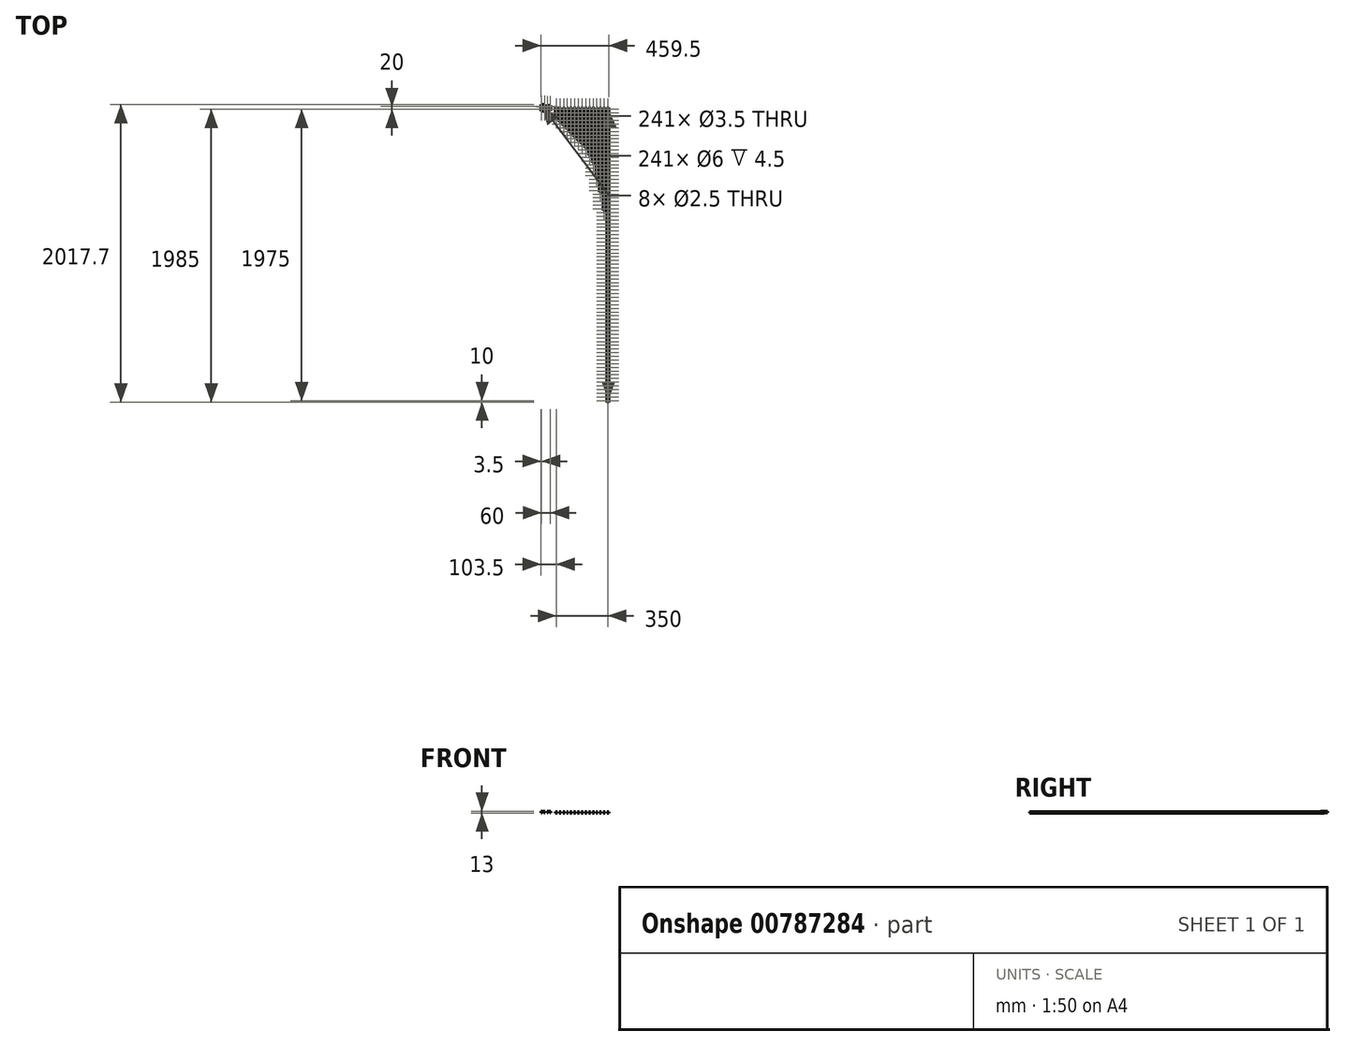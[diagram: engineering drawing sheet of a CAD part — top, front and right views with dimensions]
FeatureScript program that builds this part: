
annotation { "Feature Type Name" : "Feature", "Feature Type Description" : "" }
export const myFeature = defineFeature(function(context is Context, id is Id, definition is map)
    precondition{}
    {
        {
            var Q0;
            Q0=qCreatedBy(makeId("Front.planeOp"),FACE);
            var sketch = newSketch(context, id + "F0", { "sketchPlane" : qUnion([Q0])});
            skPoint(sketch, "E0.middle", {"position": v(0, 0) * mm});
            skLineSegment(sketch, "E1.bottom", {"start": v(5.5, -4) * mm, "end": v(-5.5, -4) * mm});
            skLineSegment(sketch, "E1.top", {"start": v(5.5, 4) * mm, "end": v(-5.5, 4) * mm});
            skLineSegment(sketch, "E1.left", {"start": v(6, -3.5) * mm, "end": v(6, -0.03) * mm});
            skLineSegment(sketch, "E1.right", {"start": v(-6, -3.5) * mm, "end": v(-6, -0.03) * mm});
            skArc(sketch, "E2", {"start": v(-6, -0.03) * mm, "mid": v(-5.5, 0.27) * mm, "end": v(-5.15, 0.75) * mm});
            skArc(sketch, "E3", {"start": v(6, 2.63) * mm, "mid": v(5.5, 2.33) * mm, "end": v(5.15, 1.85) * mm});
            skLineSegment(sketch, "E4", {"start": v(4.45, 1.85) * mm, "end": v(5.15, 1.85) * mm});
            skLineSegment(sketch, "E5", {"start": v(4.45, 0.75) * mm, "end": v(5.15, 0.75) * mm});
            skLineSegment(sketch, "E6", {"start": v(-4.45, 0.75) * mm, "end": v(-5.15, 0.75) * mm});
            skLineSegment(sketch, "E7", {"start": v(-4.45, 1.85) * mm, "end": v(-5.15, 1.85) * mm});
            skLineSegment(sketch, "E8", {"start": v(-6, 3.5) * mm, "end": v(-5.5, 4) * mm});
            skLineSegment(sketch, "E9.MirrorCS", {"start": v(6, 3.5) * mm, "end": v(5.5, 4) * mm});
            skLineSegment(sketch, "E10.MirrorCS", {"start": v(6, -3.5) * mm, "end": v(5.5, -4) * mm});
            skLineSegment(sketch, "E11.MirrorCS", {"start": v(-6, -3.5) * mm, "end": v(-5.5, -4) * mm});
            skPoint(sketch, "E12.orphan", {"position": v(-6, 4) * mm});
            skLineSegment(sketch, "E13.trimOffspring", {"start": v(-6, 2.63) * mm, "end": v(-6, 3.5) * mm});
            skArc(sketch, "E14.trimOffspring", {"start": v(-5.15, 1.85) * mm, "mid": v(-5.5, 2.33) * mm, "end": v(-6, 2.63) * mm});
            skPoint(sketch, "E15.orphan", {"position": v(6, 4) * mm});
            skLineSegment(sketch, "E16.trimOffspring", {"start": v(6, 2.63) * mm, "end": v(6, 3.5) * mm});
            skArc(sketch, "E17.trimOffspring", {"start": v(5.15, 0.75) * mm, "mid": v(5.5, 0.27) * mm, "end": v(6, -0.03) * mm});
            skPoint(sketch, "E18.orphan", {"position": v(6, -4) * mm});
            skPoint(sketch, "E19.orphan", {"position": v(-6, -4) * mm});
            skLineSegment(sketch, "E20", {"start": v(-4.45, 1.85) * mm, "end": v(-4.45, 0.75) * mm});
            skLineSegment(sketch, "E21", {"start": v(4.45, 1.85) * mm, "end": v(4.45, 0.75) * mm});
            skLineSegment(sketch, "E22", {"start": v(-6.44, 1.3) * mm, "end": v(6.44, 1.3) * mm, "construction": true});
            skLineSegment(sketch, "E23.1.0.0", {"start": v(18.56, 1.3) * mm, "end": v(31.44, 1.3) * mm, "construction": true});
            skLineSegment(sketch, "E23.1.0.1", {"start": v(19, -3.5) * mm, "end": v(19, -0.03) * mm});
            skLineSegment(sketch, "E23.1.0.2", {"start": v(31, -3.5) * mm, "end": v(31, -0.03) * mm});
            skLineSegment(sketch, "E23.1.0.3", {"start": v(30.5, -4) * mm, "end": v(19.5, -4) * mm});
            skLineSegment(sketch, "E23.1.0.4", {"start": v(30.5, 4) * mm, "end": v(19.5, 4) * mm});
            skPoint(sketch, "E23.1.0.5", {"position": v(25, 0) * mm});
            skPoint(sketch, "E23.1.0.6", {"position": v(19, -4) * mm});
            skPoint(sketch, "E23.1.0.7", {"position": v(19, 4) * mm});
            skPoint(sketch, "E23.1.0.8", {"position": v(31, 4) * mm});
            skPoint(sketch, "E23.1.0.9", {"position": v(31, -4) * mm});
            skPoint(sketch, "E23.1.0.10", {"position": v(25, 0) * mm});
            skLineSegment(sketch, "E23.1.0.11", {"start": v(31, -3.5) * mm, "end": v(30.5, -4) * mm});
            skLineSegment(sketch, "E23.1.0.12", {"start": v(31, 3.5) * mm, "end": v(30.5, 4) * mm});
            skLineSegment(sketch, "E23.1.0.13", {"start": v(19, -3.5) * mm, "end": v(19.5, -4) * mm});
            skLineSegment(sketch, "E23.1.0.14", {"start": v(20.55, 1.85) * mm, "end": v(19.85, 1.85) * mm});
            skLineSegment(sketch, "E23.1.0.15", {"start": v(19, 2.63) * mm, "end": v(19, 3.5) * mm});
            skLineSegment(sketch, "E23.1.0.16", {"start": v(31, 2.63) * mm, "end": v(31, 3.5) * mm});
            skArc(sketch, "E23.1.0.17", {"start": v(30.15, 0.75) * mm, "mid": v(30.5, 0.27) * mm, "end": v(31, -0.03) * mm});
            skLineSegment(sketch, "E23.1.0.18", {"start": v(20.55, 1.85) * mm, "end": v(20.55, 0.75) * mm});
            skLineSegment(sketch, "E23.1.0.19", {"start": v(29.45, 0.75) * mm, "end": v(30.15, 0.75) * mm});
            skLineSegment(sketch, "E23.1.0.20", {"start": v(20.55, 0.75) * mm, "end": v(19.85, 0.75) * mm});
            skArc(sketch, "E23.1.0.21", {"start": v(19, -0.03) * mm, "mid": v(19.5, 0.27) * mm, "end": v(19.85, 0.75) * mm});
            skLineSegment(sketch, "E23.1.0.22", {"start": v(19, 3.5) * mm, "end": v(19.5, 4) * mm});
            skArc(sketch, "E23.1.0.23", {"start": v(19.85, 1.85) * mm, "mid": v(19.5, 2.33) * mm, "end": v(19, 2.63) * mm});
            skLineSegment(sketch, "E23.1.0.24", {"start": v(29.45, 1.85) * mm, "end": v(30.15, 1.85) * mm});
            skArc(sketch, "E23.1.0.25", {"start": v(31, 2.63) * mm, "mid": v(30.5, 2.33) * mm, "end": v(30.15, 1.85) * mm});
            skArc(sketch, "E23.1.0.26", {"start": v(30.15, 0.75) * mm, "mid": v(30.5, 0.27) * mm, "end": v(31, -0.03) * mm});
            skLineSegment(sketch, "E23.1.0.27", {"start": v(29.45, 1.85) * mm, "end": v(29.45, 0.75) * mm});
            skLineSegment(sketch, "E23.2.0.0", {"start": v(43.56, 1.3) * mm, "end": v(56.44, 1.3) * mm, "construction": true});
            skLineSegment(sketch, "E23.2.0.1", {"start": v(44, -3.5) * mm, "end": v(44, -0.03) * mm});
            skLineSegment(sketch, "E23.2.0.2", {"start": v(56, -3.5) * mm, "end": v(56, -0.03) * mm});
            skLineSegment(sketch, "E23.2.0.3", {"start": v(55.5, -4) * mm, "end": v(44.5, -4) * mm});
            skLineSegment(sketch, "E23.2.0.4", {"start": v(55.5, 4) * mm, "end": v(44.5, 4) * mm});
            skPoint(sketch, "E23.2.0.5", {"position": v(50, 0) * mm});
            skPoint(sketch, "E23.2.0.6", {"position": v(44, -4) * mm});
            skPoint(sketch, "E23.2.0.7", {"position": v(44, 4) * mm});
            skPoint(sketch, "E23.2.0.8", {"position": v(56, 4) * mm});
            skPoint(sketch, "E23.2.0.9", {"position": v(56, -4) * mm});
            skPoint(sketch, "E23.2.0.10", {"position": v(50, 0) * mm});
            skLineSegment(sketch, "E23.2.0.11", {"start": v(56, -3.5) * mm, "end": v(55.5, -4) * mm});
            skLineSegment(sketch, "E23.2.0.12", {"start": v(56, 3.5) * mm, "end": v(55.5, 4) * mm});
            skLineSegment(sketch, "E23.2.0.13", {"start": v(44, -3.5) * mm, "end": v(44.5, -4) * mm});
            skLineSegment(sketch, "E23.2.0.14", {"start": v(45.55, 1.85) * mm, "end": v(44.85, 1.85) * mm});
            skLineSegment(sketch, "E23.2.0.15", {"start": v(44, 2.63) * mm, "end": v(44, 3.5) * mm});
            skLineSegment(sketch, "E23.2.0.16", {"start": v(56, 2.63) * mm, "end": v(56, 3.5) * mm});
            skArc(sketch, "E23.2.0.17", {"start": v(55.15, 0.75) * mm, "mid": v(55.5, 0.27) * mm, "end": v(56, -0.03) * mm});
            skLineSegment(sketch, "E23.2.0.18", {"start": v(45.55, 1.85) * mm, "end": v(45.55, 0.75) * mm});
            skLineSegment(sketch, "E23.2.0.19", {"start": v(54.45, 0.75) * mm, "end": v(55.15, 0.75) * mm});
            skLineSegment(sketch, "E23.2.0.20", {"start": v(45.55, 0.75) * mm, "end": v(44.85, 0.75) * mm});
            skArc(sketch, "E23.2.0.21", {"start": v(44, -0.03) * mm, "mid": v(44.5, 0.27) * mm, "end": v(44.85, 0.75) * mm});
            skLineSegment(sketch, "E23.2.0.22", {"start": v(44, 3.5) * mm, "end": v(44.5, 4) * mm});
            skArc(sketch, "E23.2.0.23", {"start": v(44.85, 1.85) * mm, "mid": v(44.5, 2.33) * mm, "end": v(44, 2.63) * mm});
            skLineSegment(sketch, "E23.2.0.24", {"start": v(54.45, 1.85) * mm, "end": v(55.15, 1.85) * mm});
            skArc(sketch, "E23.2.0.25", {"start": v(56, 2.63) * mm, "mid": v(55.5, 2.33) * mm, "end": v(55.15, 1.85) * mm});
            skArc(sketch, "E23.2.0.26", {"start": v(55.15, 0.75) * mm, "mid": v(55.5, 0.27) * mm, "end": v(56, -0.03) * mm});
            skLineSegment(sketch, "E23.2.0.27", {"start": v(54.45, 1.85) * mm, "end": v(54.45, 0.75) * mm});
            skLineSegment(sketch, "E23.3.0.0", {"start": v(68.56, 1.3) * mm, "end": v(81.44, 1.3) * mm, "construction": true});
            skLineSegment(sketch, "E23.3.0.1", {"start": v(69, -3.5) * mm, "end": v(69, -0.03) * mm});
            skLineSegment(sketch, "E23.3.0.2", {"start": v(81, -3.5) * mm, "end": v(81, -0.03) * mm});
            skLineSegment(sketch, "E23.3.0.3", {"start": v(80.5, -4) * mm, "end": v(69.5, -4) * mm});
            skLineSegment(sketch, "E23.3.0.4", {"start": v(80.5, 4) * mm, "end": v(69.5, 4) * mm});
            skPoint(sketch, "E23.3.0.5", {"position": v(75, 0) * mm});
            skPoint(sketch, "E23.3.0.6", {"position": v(69, -4) * mm});
            skPoint(sketch, "E23.3.0.7", {"position": v(69, 4) * mm});
            skPoint(sketch, "E23.3.0.8", {"position": v(81, 4) * mm});
            skPoint(sketch, "E23.3.0.9", {"position": v(81, -4) * mm});
            skPoint(sketch, "E23.3.0.10", {"position": v(75, 0) * mm});
            skLineSegment(sketch, "E23.3.0.11", {"start": v(81, -3.5) * mm, "end": v(80.5, -4) * mm});
            skLineSegment(sketch, "E23.3.0.12", {"start": v(81, 3.5) * mm, "end": v(80.5, 4) * mm});
            skLineSegment(sketch, "E23.3.0.13", {"start": v(69, -3.5) * mm, "end": v(69.5, -4) * mm});
            skLineSegment(sketch, "E23.3.0.14", {"start": v(70.55, 1.85) * mm, "end": v(69.85, 1.85) * mm});
            skLineSegment(sketch, "E23.3.0.15", {"start": v(69, 2.63) * mm, "end": v(69, 3.5) * mm});
            skLineSegment(sketch, "E23.3.0.16", {"start": v(81, 2.63) * mm, "end": v(81, 3.5) * mm});
            skArc(sketch, "E23.3.0.17", {"start": v(80.15, 0.75) * mm, "mid": v(80.5, 0.27) * mm, "end": v(81, -0.03) * mm});
            skLineSegment(sketch, "E23.3.0.18", {"start": v(70.55, 1.85) * mm, "end": v(70.55, 0.75) * mm});
            skLineSegment(sketch, "E23.3.0.19", {"start": v(79.45, 0.75) * mm, "end": v(80.15, 0.75) * mm});
            skLineSegment(sketch, "E23.3.0.20", {"start": v(70.55, 0.75) * mm, "end": v(69.85, 0.75) * mm});
            skArc(sketch, "E23.3.0.21", {"start": v(69, -0.03) * mm, "mid": v(69.5, 0.27) * mm, "end": v(69.85, 0.75) * mm});
            skLineSegment(sketch, "E23.3.0.22", {"start": v(69, 3.5) * mm, "end": v(69.5, 4) * mm});
            skArc(sketch, "E23.3.0.23", {"start": v(69.85, 1.85) * mm, "mid": v(69.5, 2.33) * mm, "end": v(69, 2.63) * mm});
            skLineSegment(sketch, "E23.3.0.24", {"start": v(79.45, 1.85) * mm, "end": v(80.15, 1.85) * mm});
            skArc(sketch, "E23.3.0.25", {"start": v(81, 2.63) * mm, "mid": v(80.5, 2.33) * mm, "end": v(80.15, 1.85) * mm});
            skArc(sketch, "E23.3.0.26", {"start": v(80.15, 0.75) * mm, "mid": v(80.5, 0.27) * mm, "end": v(81, -0.03) * mm});
            skLineSegment(sketch, "E23.3.0.27", {"start": v(79.45, 1.85) * mm, "end": v(79.45, 0.75) * mm});
            skLineSegment(sketch, "E23.4.0.0", {"start": v(93.56, 1.3) * mm, "end": v(106.44, 1.3) * mm, "construction": true});
            skLineSegment(sketch, "E23.4.0.1", {"start": v(94, -3.5) * mm, "end": v(94, -0.03) * mm});
            skLineSegment(sketch, "E23.4.0.2", {"start": v(106, -3.5) * mm, "end": v(106, -0.03) * mm});
            skLineSegment(sketch, "E23.4.0.3", {"start": v(105.5, -4) * mm, "end": v(94.5, -4) * mm});
            skLineSegment(sketch, "E23.4.0.4", {"start": v(105.5, 4) * mm, "end": v(94.5, 4) * mm});
            skPoint(sketch, "E23.4.0.5", {"position": v(100, 0) * mm});
            skPoint(sketch, "E23.4.0.6", {"position": v(94, -4) * mm});
            skPoint(sketch, "E23.4.0.7", {"position": v(94, 4) * mm});
            skPoint(sketch, "E23.4.0.8", {"position": v(106, 4) * mm});
            skPoint(sketch, "E23.4.0.9", {"position": v(106, -4) * mm});
            skPoint(sketch, "E23.4.0.10", {"position": v(100, 0) * mm});
            skLineSegment(sketch, "E23.4.0.11", {"start": v(106, -3.5) * mm, "end": v(105.5, -4) * mm});
            skLineSegment(sketch, "E23.4.0.12", {"start": v(106, 3.5) * mm, "end": v(105.5, 4) * mm});
            skLineSegment(sketch, "E23.4.0.13", {"start": v(94, -3.5) * mm, "end": v(94.5, -4) * mm});
            skLineSegment(sketch, "E23.4.0.14", {"start": v(95.55, 1.85) * mm, "end": v(94.85, 1.85) * mm});
            skLineSegment(sketch, "E23.4.0.15", {"start": v(94, 2.63) * mm, "end": v(94, 3.5) * mm});
            skLineSegment(sketch, "E23.4.0.16", {"start": v(106, 2.63) * mm, "end": v(106, 3.5) * mm});
            skArc(sketch, "E23.4.0.17", {"start": v(105.15, 0.75) * mm, "mid": v(105.5, 0.27) * mm, "end": v(106, -0.03) * mm});
            skLineSegment(sketch, "E23.4.0.18", {"start": v(95.55, 1.85) * mm, "end": v(95.55, 0.75) * mm});
            skLineSegment(sketch, "E23.4.0.19", {"start": v(104.45, 0.75) * mm, "end": v(105.15, 0.75) * mm});
            skLineSegment(sketch, "E23.4.0.20", {"start": v(95.55, 0.75) * mm, "end": v(94.85, 0.75) * mm});
            skArc(sketch, "E23.4.0.21", {"start": v(94, -0.03) * mm, "mid": v(94.5, 0.27) * mm, "end": v(94.85, 0.75) * mm});
            skLineSegment(sketch, "E23.4.0.22", {"start": v(94, 3.5) * mm, "end": v(94.5, 4) * mm});
            skArc(sketch, "E23.4.0.23", {"start": v(94.85, 1.85) * mm, "mid": v(94.5, 2.33) * mm, "end": v(94, 2.63) * mm});
            skLineSegment(sketch, "E23.4.0.24", {"start": v(104.45, 1.85) * mm, "end": v(105.15, 1.85) * mm});
            skArc(sketch, "E23.4.0.25", {"start": v(106, 2.63) * mm, "mid": v(105.5, 2.33) * mm, "end": v(105.15, 1.85) * mm});
            skArc(sketch, "E23.4.0.26", {"start": v(105.15, 0.75) * mm, "mid": v(105.5, 0.27) * mm, "end": v(106, -0.03) * mm});
            skLineSegment(sketch, "E23.4.0.27", {"start": v(104.45, 1.85) * mm, "end": v(104.45, 0.75) * mm});
            skLineSegment(sketch, "E23.5.0.0", {"start": v(118.56, 1.3) * mm, "end": v(131.44, 1.3) * mm, "construction": true});
            skLineSegment(sketch, "E23.5.0.1", {"start": v(119, -3.5) * mm, "end": v(119, -0.03) * mm});
            skLineSegment(sketch, "E23.5.0.2", {"start": v(131, -3.5) * mm, "end": v(131, -0.03) * mm});
            skLineSegment(sketch, "E23.5.0.3", {"start": v(130.5, -4) * mm, "end": v(119.5, -4) * mm});
            skLineSegment(sketch, "E23.5.0.4", {"start": v(130.5, 4) * mm, "end": v(119.5, 4) * mm});
            skPoint(sketch, "E23.5.0.5", {"position": v(125, 0) * mm});
            skPoint(sketch, "E23.5.0.6", {"position": v(119, -4) * mm});
            skPoint(sketch, "E23.5.0.7", {"position": v(119, 4) * mm});
            skPoint(sketch, "E23.5.0.8", {"position": v(131, 4) * mm});
            skPoint(sketch, "E23.5.0.9", {"position": v(131, -4) * mm});
            skPoint(sketch, "E23.5.0.10", {"position": v(125, 0) * mm});
            skLineSegment(sketch, "E23.5.0.11", {"start": v(131, -3.5) * mm, "end": v(130.5, -4) * mm});
            skLineSegment(sketch, "E23.5.0.12", {"start": v(131, 3.5) * mm, "end": v(130.5, 4) * mm});
            skLineSegment(sketch, "E23.5.0.13", {"start": v(119, -3.5) * mm, "end": v(119.5, -4) * mm});
            skLineSegment(sketch, "E23.5.0.14", {"start": v(120.55, 1.85) * mm, "end": v(119.85, 1.85) * mm});
            skLineSegment(sketch, "E23.5.0.15", {"start": v(119, 2.63) * mm, "end": v(119, 3.5) * mm});
            skLineSegment(sketch, "E23.5.0.16", {"start": v(131, 2.63) * mm, "end": v(131, 3.5) * mm});
            skArc(sketch, "E23.5.0.17", {"start": v(130.15, 0.75) * mm, "mid": v(130.5, 0.27) * mm, "end": v(131, -0.03) * mm});
            skLineSegment(sketch, "E23.5.0.18", {"start": v(120.55, 1.85) * mm, "end": v(120.55, 0.75) * mm});
            skLineSegment(sketch, "E23.5.0.19", {"start": v(129.45, 0.75) * mm, "end": v(130.15, 0.75) * mm});
            skLineSegment(sketch, "E23.5.0.20", {"start": v(120.55, 0.75) * mm, "end": v(119.85, 0.75) * mm});
            skArc(sketch, "E23.5.0.21", {"start": v(119, -0.03) * mm, "mid": v(119.5, 0.27) * mm, "end": v(119.85, 0.75) * mm});
            skLineSegment(sketch, "E23.5.0.22", {"start": v(119, 3.5) * mm, "end": v(119.5, 4) * mm});
            skArc(sketch, "E23.5.0.23", {"start": v(119.85, 1.85) * mm, "mid": v(119.5, 2.33) * mm, "end": v(119, 2.63) * mm});
            skLineSegment(sketch, "E23.5.0.24", {"start": v(129.45, 1.85) * mm, "end": v(130.15, 1.85) * mm});
            skArc(sketch, "E23.5.0.25", {"start": v(131, 2.63) * mm, "mid": v(130.5, 2.33) * mm, "end": v(130.15, 1.85) * mm});
            skArc(sketch, "E23.5.0.26", {"start": v(130.15, 0.75) * mm, "mid": v(130.5, 0.27) * mm, "end": v(131, -0.03) * mm});
            skLineSegment(sketch, "E23.5.0.27", {"start": v(129.45, 1.85) * mm, "end": v(129.45, 0.75) * mm});
            skLineSegment(sketch, "E23.6.0.0", {"start": v(143.56, 1.3) * mm, "end": v(156.44, 1.3) * mm, "construction": true});
            skLineSegment(sketch, "E23.6.0.1", {"start": v(144, -3.5) * mm, "end": v(144, -0.03) * mm});
            skLineSegment(sketch, "E23.6.0.2", {"start": v(156, -3.5) * mm, "end": v(156, -0.03) * mm});
            skLineSegment(sketch, "E23.6.0.3", {"start": v(155.5, -4) * mm, "end": v(144.5, -4) * mm});
            skLineSegment(sketch, "E23.6.0.4", {"start": v(155.5, 4) * mm, "end": v(144.5, 4) * mm});
            skPoint(sketch, "E23.6.0.5", {"position": v(150, 0) * mm});
            skPoint(sketch, "E23.6.0.6", {"position": v(144, -4) * mm});
            skPoint(sketch, "E23.6.0.7", {"position": v(144, 4) * mm});
            skPoint(sketch, "E23.6.0.8", {"position": v(156, 4) * mm});
            skPoint(sketch, "E23.6.0.9", {"position": v(156, -4) * mm});
            skPoint(sketch, "E23.6.0.10", {"position": v(150, 0) * mm});
            skLineSegment(sketch, "E23.6.0.11", {"start": v(156, -3.5) * mm, "end": v(155.5, -4) * mm});
            skLineSegment(sketch, "E23.6.0.12", {"start": v(156, 3.5) * mm, "end": v(155.5, 4) * mm});
            skLineSegment(sketch, "E23.6.0.13", {"start": v(144, -3.5) * mm, "end": v(144.5, -4) * mm});
            skLineSegment(sketch, "E23.6.0.14", {"start": v(145.55, 1.85) * mm, "end": v(144.85, 1.85) * mm});
            skLineSegment(sketch, "E23.6.0.15", {"start": v(144, 2.63) * mm, "end": v(144, 3.5) * mm});
            skLineSegment(sketch, "E23.6.0.16", {"start": v(156, 2.63) * mm, "end": v(156, 3.5) * mm});
            skArc(sketch, "E23.6.0.17", {"start": v(155.15, 0.75) * mm, "mid": v(155.5, 0.27) * mm, "end": v(156, -0.03) * mm});
            skLineSegment(sketch, "E23.6.0.18", {"start": v(145.55, 1.85) * mm, "end": v(145.55, 0.75) * mm});
            skLineSegment(sketch, "E23.6.0.19", {"start": v(154.45, 0.75) * mm, "end": v(155.15, 0.75) * mm});
            skLineSegment(sketch, "E23.6.0.20", {"start": v(145.55, 0.75) * mm, "end": v(144.85, 0.75) * mm});
            skArc(sketch, "E23.6.0.21", {"start": v(144, -0.03) * mm, "mid": v(144.5, 0.27) * mm, "end": v(144.85, 0.75) * mm});
            skLineSegment(sketch, "E23.6.0.22", {"start": v(144, 3.5) * mm, "end": v(144.5, 4) * mm});
            skArc(sketch, "E23.6.0.23", {"start": v(144.85, 1.85) * mm, "mid": v(144.5, 2.33) * mm, "end": v(144, 2.63) * mm});
            skLineSegment(sketch, "E23.6.0.24", {"start": v(154.45, 1.85) * mm, "end": v(155.15, 1.85) * mm});
            skArc(sketch, "E23.6.0.25", {"start": v(156, 2.63) * mm, "mid": v(155.5, 2.33) * mm, "end": v(155.15, 1.85) * mm});
            skArc(sketch, "E23.6.0.26", {"start": v(155.15, 0.75) * mm, "mid": v(155.5, 0.27) * mm, "end": v(156, -0.03) * mm});
            skLineSegment(sketch, "E23.6.0.27", {"start": v(154.45, 1.85) * mm, "end": v(154.45, 0.75) * mm});
            skLineSegment(sketch, "E23.direction1", {"start": v(-6, -4) * mm, "end": v(19, -4) * mm, "construction": true});
            skLineSegment(sketch, "E24.0.7.0", {"start": v(168.56, 1.3) * mm, "end": v(181.44, 1.3) * mm, "construction": true});
            skLineSegment(sketch, "E24.3.7.0", {"start": v(169, -3.5) * mm, "end": v(169, -0.03) * mm});
            skLineSegment(sketch, "E24.6.7.0", {"start": v(181, -3.5) * mm, "end": v(181, -0.03) * mm});
            skLineSegment(sketch, "E24.9.7.0", {"start": v(180.5, -4) * mm, "end": v(169.5, -4) * mm});
            skLineSegment(sketch, "E24.12.7.0", {"start": v(180.5, 4) * mm, "end": v(169.5, 4) * mm});
            skPoint(sketch, "E24.15.7.0", {"position": v(175, 0) * mm});
            skPoint(sketch, "E24.16.7.0", {"position": v(169, -4) * mm});
            skPoint(sketch, "E24.17.7.0", {"position": v(169, 4) * mm});
            skPoint(sketch, "E24.18.7.0", {"position": v(181, 4) * mm});
            skPoint(sketch, "E24.19.7.0", {"position": v(181, -4) * mm});
            skPoint(sketch, "E24.20.7.0", {"position": v(175, 0) * mm});
            skLineSegment(sketch, "E24.21.7.0", {"start": v(181, -3.5) * mm, "end": v(180.5, -4) * mm});
            skLineSegment(sketch, "E24.24.7.0", {"start": v(181, 3.5) * mm, "end": v(180.5, 4) * mm});
            skLineSegment(sketch, "E24.27.7.0", {"start": v(169, -3.5) * mm, "end": v(169.5, -4) * mm});
            skLineSegment(sketch, "E24.30.7.0", {"start": v(170.55, 1.85) * mm, "end": v(169.85, 1.85) * mm});
            skLineSegment(sketch, "E24.33.7.0", {"start": v(169, 2.63) * mm, "end": v(169, 3.5) * mm});
            skLineSegment(sketch, "E24.36.7.0", {"start": v(181, 2.63) * mm, "end": v(181, 3.5) * mm});
            skArc(sketch, "E24.39.7.0", {"start": v(180.15, 0.75) * mm, "mid": v(180.5, 0.27) * mm, "end": v(181, -0.03) * mm});
            skLineSegment(sketch, "E24.43.7.0", {"start": v(170.55, 1.85) * mm, "end": v(170.55, 0.75) * mm});
            skLineSegment(sketch, "E24.46.7.0", {"start": v(179.45, 0.75) * mm, "end": v(180.15, 0.75) * mm});
            skLineSegment(sketch, "E24.49.7.0", {"start": v(170.55, 0.75) * mm, "end": v(169.85, 0.75) * mm});
            skArc(sketch, "E24.52.7.0", {"start": v(169, -0.03) * mm, "mid": v(169.5, 0.27) * mm, "end": v(169.85, 0.75) * mm});
            skLineSegment(sketch, "E24.56.7.0", {"start": v(169, 3.5) * mm, "end": v(169.5, 4) * mm});
            skArc(sketch, "E24.59.7.0", {"start": v(169.85, 1.85) * mm, "mid": v(169.5, 2.33) * mm, "end": v(169, 2.63) * mm});
            skLineSegment(sketch, "E24.63.7.0", {"start": v(179.45, 1.85) * mm, "end": v(180.15, 1.85) * mm});
            skArc(sketch, "E24.66.7.0", {"start": v(181, 2.63) * mm, "mid": v(180.5, 2.33) * mm, "end": v(180.15, 1.85) * mm});
            skArc(sketch, "E24.70.7.0", {"start": v(180.15, 0.75) * mm, "mid": v(180.5, 0.27) * mm, "end": v(181, -0.03) * mm});
            skLineSegment(sketch, "E24.74.7.0", {"start": v(179.45, 1.85) * mm, "end": v(179.45, 0.75) * mm});
            skLineSegment(sketch, "E24.0.8.0", {"start": v(193.56, 1.3) * mm, "end": v(206.44, 1.3) * mm, "construction": true});
            skLineSegment(sketch, "E24.3.8.0", {"start": v(194, -3.5) * mm, "end": v(194, -0.03) * mm});
            skLineSegment(sketch, "E24.6.8.0", {"start": v(206, -3.5) * mm, "end": v(206, -0.03) * mm});
            skLineSegment(sketch, "E24.9.8.0", {"start": v(205.5, -4) * mm, "end": v(194.5, -4) * mm});
            skLineSegment(sketch, "E24.12.8.0", {"start": v(205.5, 4) * mm, "end": v(194.5, 4) * mm});
            skPoint(sketch, "E24.15.8.0", {"position": v(200, 0) * mm});
            skPoint(sketch, "E24.16.8.0", {"position": v(194, -4) * mm});
            skPoint(sketch, "E24.17.8.0", {"position": v(194, 4) * mm});
            skPoint(sketch, "E24.18.8.0", {"position": v(206, 4) * mm});
            skPoint(sketch, "E24.19.8.0", {"position": v(206, -4) * mm});
            skPoint(sketch, "E24.20.8.0", {"position": v(200, 0) * mm});
            skLineSegment(sketch, "E24.21.8.0", {"start": v(206, -3.5) * mm, "end": v(205.5, -4) * mm});
            skLineSegment(sketch, "E24.24.8.0", {"start": v(206, 3.5) * mm, "end": v(205.5, 4) * mm});
            skLineSegment(sketch, "E24.27.8.0", {"start": v(194, -3.5) * mm, "end": v(194.5, -4) * mm});
            skLineSegment(sketch, "E24.30.8.0", {"start": v(195.55, 1.85) * mm, "end": v(194.85, 1.85) * mm});
            skLineSegment(sketch, "E24.33.8.0", {"start": v(194, 2.63) * mm, "end": v(194, 3.5) * mm});
            skLineSegment(sketch, "E24.36.8.0", {"start": v(206, 2.63) * mm, "end": v(206, 3.5) * mm});
            skArc(sketch, "E24.39.8.0", {"start": v(205.15, 0.75) * mm, "mid": v(205.5, 0.27) * mm, "end": v(206, -0.03) * mm});
            skLineSegment(sketch, "E24.43.8.0", {"start": v(195.55, 1.85) * mm, "end": v(195.55, 0.75) * mm});
            skLineSegment(sketch, "E24.46.8.0", {"start": v(204.45, 0.75) * mm, "end": v(205.15, 0.75) * mm});
            skLineSegment(sketch, "E24.49.8.0", {"start": v(195.55, 0.75) * mm, "end": v(194.85, 0.75) * mm});
            skArc(sketch, "E24.52.8.0", {"start": v(194, -0.03) * mm, "mid": v(194.5, 0.27) * mm, "end": v(194.85, 0.75) * mm});
            skLineSegment(sketch, "E24.56.8.0", {"start": v(194, 3.5) * mm, "end": v(194.5, 4) * mm});
            skArc(sketch, "E24.59.8.0", {"start": v(194.85, 1.85) * mm, "mid": v(194.5, 2.33) * mm, "end": v(194, 2.63) * mm});
            skLineSegment(sketch, "E24.63.8.0", {"start": v(204.45, 1.85) * mm, "end": v(205.15, 1.85) * mm});
            skArc(sketch, "E24.66.8.0", {"start": v(206, 2.63) * mm, "mid": v(205.5, 2.33) * mm, "end": v(205.15, 1.85) * mm});
            skArc(sketch, "E24.70.8.0", {"start": v(205.15, 0.75) * mm, "mid": v(205.5, 0.27) * mm, "end": v(206, -0.03) * mm});
            skLineSegment(sketch, "E24.74.8.0", {"start": v(204.45, 1.85) * mm, "end": v(204.45, 0.75) * mm});
            skLineSegment(sketch, "E24.0.9.0", {"start": v(218.56, 1.3) * mm, "end": v(231.44, 1.3) * mm, "construction": true});
            skLineSegment(sketch, "E24.3.9.0", {"start": v(219, -3.5) * mm, "end": v(219, -0.03) * mm});
            skLineSegment(sketch, "E24.6.9.0", {"start": v(231, -3.5) * mm, "end": v(231, -0.03) * mm});
            skLineSegment(sketch, "E24.9.9.0", {"start": v(230.5, -4) * mm, "end": v(219.5, -4) * mm});
            skLineSegment(sketch, "E24.12.9.0", {"start": v(230.5, 4) * mm, "end": v(219.5, 4) * mm});
            skPoint(sketch, "E24.15.9.0", {"position": v(225, 0) * mm});
            skPoint(sketch, "E24.16.9.0", {"position": v(219, -4) * mm});
            skPoint(sketch, "E24.17.9.0", {"position": v(219, 4) * mm});
            skPoint(sketch, "E24.18.9.0", {"position": v(231, 4) * mm});
            skPoint(sketch, "E24.19.9.0", {"position": v(231, -4) * mm});
            skPoint(sketch, "E24.20.9.0", {"position": v(225, 0) * mm});
            skLineSegment(sketch, "E24.21.9.0", {"start": v(231, -3.5) * mm, "end": v(230.5, -4) * mm});
            skLineSegment(sketch, "E24.24.9.0", {"start": v(231, 3.5) * mm, "end": v(230.5, 4) * mm});
            skLineSegment(sketch, "E24.27.9.0", {"start": v(219, -3.5) * mm, "end": v(219.5, -4) * mm});
            skLineSegment(sketch, "E24.30.9.0", {"start": v(220.55, 1.85) * mm, "end": v(219.85, 1.85) * mm});
            skLineSegment(sketch, "E24.33.9.0", {"start": v(219, 2.63) * mm, "end": v(219, 3.5) * mm});
            skLineSegment(sketch, "E24.36.9.0", {"start": v(231, 2.63) * mm, "end": v(231, 3.5) * mm});
            skArc(sketch, "E24.39.9.0", {"start": v(230.15, 0.75) * mm, "mid": v(230.5, 0.27) * mm, "end": v(231, -0.03) * mm});
            skLineSegment(sketch, "E24.43.9.0", {"start": v(220.55, 1.85) * mm, "end": v(220.55, 0.75) * mm});
            skLineSegment(sketch, "E24.46.9.0", {"start": v(229.45, 0.75) * mm, "end": v(230.15, 0.75) * mm});
            skLineSegment(sketch, "E24.49.9.0", {"start": v(220.55, 0.75) * mm, "end": v(219.85, 0.75) * mm});
            skArc(sketch, "E24.52.9.0", {"start": v(219, -0.03) * mm, "mid": v(219.5, 0.27) * mm, "end": v(219.85, 0.75) * mm});
            skLineSegment(sketch, "E24.56.9.0", {"start": v(219, 3.5) * mm, "end": v(219.5, 4) * mm});
            skArc(sketch, "E24.59.9.0", {"start": v(219.85, 1.85) * mm, "mid": v(219.5, 2.33) * mm, "end": v(219, 2.63) * mm});
            skLineSegment(sketch, "E24.63.9.0", {"start": v(229.45, 1.85) * mm, "end": v(230.15, 1.85) * mm});
            skArc(sketch, "E24.66.9.0", {"start": v(231, 2.63) * mm, "mid": v(230.5, 2.33) * mm, "end": v(230.15, 1.85) * mm});
            skArc(sketch, "E24.70.9.0", {"start": v(230.15, 0.75) * mm, "mid": v(230.5, 0.27) * mm, "end": v(231, -0.03) * mm});
            skLineSegment(sketch, "E24.74.9.0", {"start": v(229.45, 1.85) * mm, "end": v(229.45, 0.75) * mm});
            skLineSegment(sketch, "E24.0.10.0", {"start": v(243.56, 1.3) * mm, "end": v(256.44, 1.3) * mm, "construction": true});
            skLineSegment(sketch, "E24.3.10.0", {"start": v(244, -3.5) * mm, "end": v(244, -0.03) * mm});
            skLineSegment(sketch, "E24.6.10.0", {"start": v(256, -3.5) * mm, "end": v(256, -0.03) * mm});
            skLineSegment(sketch, "E24.9.10.0", {"start": v(255.5, -4) * mm, "end": v(244.5, -4) * mm});
            skLineSegment(sketch, "E24.12.10.0", {"start": v(255.5, 4) * mm, "end": v(244.5, 4) * mm});
            skPoint(sketch, "E24.15.10.0", {"position": v(250, 0) * mm});
            skPoint(sketch, "E24.16.10.0", {"position": v(244, -4) * mm});
            skPoint(sketch, "E24.17.10.0", {"position": v(244, 4) * mm});
            skPoint(sketch, "E24.18.10.0", {"position": v(256, 4) * mm});
            skPoint(sketch, "E24.19.10.0", {"position": v(256, -4) * mm});
            skPoint(sketch, "E24.20.10.0", {"position": v(250, 0) * mm});
            skLineSegment(sketch, "E24.21.10.0", {"start": v(256, -3.5) * mm, "end": v(255.5, -4) * mm});
            skLineSegment(sketch, "E24.24.10.0", {"start": v(256, 3.5) * mm, "end": v(255.5, 4) * mm});
            skLineSegment(sketch, "E24.27.10.0", {"start": v(244, -3.5) * mm, "end": v(244.5, -4) * mm});
            skLineSegment(sketch, "E24.30.10.0", {"start": v(245.55, 1.85) * mm, "end": v(244.85, 1.85) * mm});
            skLineSegment(sketch, "E24.33.10.0", {"start": v(244, 2.63) * mm, "end": v(244, 3.5) * mm});
            skLineSegment(sketch, "E24.36.10.0", {"start": v(256, 2.63) * mm, "end": v(256, 3.5) * mm});
            skArc(sketch, "E24.39.10.0", {"start": v(255.15, 0.75) * mm, "mid": v(255.5, 0.27) * mm, "end": v(256, -0.03) * mm});
            skLineSegment(sketch, "E24.43.10.0", {"start": v(245.55, 1.85) * mm, "end": v(245.55, 0.75) * mm});
            skLineSegment(sketch, "E24.46.10.0", {"start": v(254.45, 0.75) * mm, "end": v(255.15, 0.75) * mm});
            skLineSegment(sketch, "E24.49.10.0", {"start": v(245.55, 0.75) * mm, "end": v(244.85, 0.75) * mm});
            skArc(sketch, "E24.52.10.0", {"start": v(244, -0.03) * mm, "mid": v(244.5, 0.27) * mm, "end": v(244.85, 0.75) * mm});
            skLineSegment(sketch, "E24.56.10.0", {"start": v(244, 3.5) * mm, "end": v(244.5, 4) * mm});
            skArc(sketch, "E24.59.10.0", {"start": v(244.85, 1.85) * mm, "mid": v(244.5, 2.33) * mm, "end": v(244, 2.63) * mm});
            skLineSegment(sketch, "E24.63.10.0", {"start": v(254.45, 1.85) * mm, "end": v(255.15, 1.85) * mm});
            skArc(sketch, "E24.66.10.0", {"start": v(256, 2.63) * mm, "mid": v(255.5, 2.33) * mm, "end": v(255.15, 1.85) * mm});
            skArc(sketch, "E24.70.10.0", {"start": v(255.15, 0.75) * mm, "mid": v(255.5, 0.27) * mm, "end": v(256, -0.03) * mm});
            skLineSegment(sketch, "E24.74.10.0", {"start": v(254.45, 1.85) * mm, "end": v(254.45, 0.75) * mm});
            skLineSegment(sketch, "E25.0.11.0", {"start": v(268.56, 1.3) * mm, "end": v(281.44, 1.3) * mm, "construction": true});
            skLineSegment(sketch, "E25.3.11.0", {"start": v(269, -3.5) * mm, "end": v(269, -0.03) * mm});
            skLineSegment(sketch, "E25.6.11.0", {"start": v(281, -3.5) * mm, "end": v(281, -0.03) * mm});
            skLineSegment(sketch, "E25.9.11.0", {"start": v(280.5, -4) * mm, "end": v(269.5, -4) * mm});
            skLineSegment(sketch, "E25.12.11.0", {"start": v(280.5, 4) * mm, "end": v(269.5, 4) * mm});
            skPoint(sketch, "E25.15.11.0", {"position": v(275, 0) * mm});
            skPoint(sketch, "E25.16.11.0", {"position": v(269, -4) * mm});
            skPoint(sketch, "E25.17.11.0", {"position": v(269, 4) * mm});
            skPoint(sketch, "E25.18.11.0", {"position": v(281, 4) * mm});
            skPoint(sketch, "E25.19.11.0", {"position": v(281, -4) * mm});
            skPoint(sketch, "E25.20.11.0", {"position": v(275, 0) * mm});
            skLineSegment(sketch, "E25.21.11.0", {"start": v(281, -3.5) * mm, "end": v(280.5, -4) * mm});
            skLineSegment(sketch, "E25.24.11.0", {"start": v(281, 3.5) * mm, "end": v(280.5, 4) * mm});
            skLineSegment(sketch, "E25.27.11.0", {"start": v(269, -3.5) * mm, "end": v(269.5, -4) * mm});
            skLineSegment(sketch, "E25.30.11.0", {"start": v(270.55, 1.85) * mm, "end": v(269.85, 1.85) * mm});
            skLineSegment(sketch, "E25.33.11.0", {"start": v(269, 2.63) * mm, "end": v(269, 3.5) * mm});
            skLineSegment(sketch, "E25.36.11.0", {"start": v(281, 2.63) * mm, "end": v(281, 3.5) * mm});
            skArc(sketch, "E25.39.11.0", {"start": v(280.15, 0.75) * mm, "mid": v(280.5, 0.27) * mm, "end": v(281, -0.03) * mm});
            skLineSegment(sketch, "E25.43.11.0", {"start": v(270.55, 1.85) * mm, "end": v(270.55, 0.75) * mm});
            skLineSegment(sketch, "E25.46.11.0", {"start": v(279.45, 0.75) * mm, "end": v(280.15, 0.75) * mm});
            skLineSegment(sketch, "E25.49.11.0", {"start": v(270.55, 0.75) * mm, "end": v(269.85, 0.75) * mm});
            skArc(sketch, "E25.52.11.0", {"start": v(269, -0.03) * mm, "mid": v(269.5, 0.27) * mm, "end": v(269.85, 0.75) * mm});
            skLineSegment(sketch, "E25.56.11.0", {"start": v(269, 3.5) * mm, "end": v(269.5, 4) * mm});
            skArc(sketch, "E25.59.11.0", {"start": v(269.85, 1.85) * mm, "mid": v(269.5, 2.33) * mm, "end": v(269, 2.63) * mm});
            skLineSegment(sketch, "E25.63.11.0", {"start": v(279.45, 1.85) * mm, "end": v(280.15, 1.85) * mm});
            skArc(sketch, "E25.66.11.0", {"start": v(281, 2.63) * mm, "mid": v(280.5, 2.33) * mm, "end": v(280.15, 1.85) * mm});
            skArc(sketch, "E25.70.11.0", {"start": v(280.15, 0.75) * mm, "mid": v(280.5, 0.27) * mm, "end": v(281, -0.03) * mm});
            skLineSegment(sketch, "E25.74.11.0", {"start": v(279.45, 1.85) * mm, "end": v(279.45, 0.75) * mm});
            skLineSegment(sketch, "E25.0.12.0", {"start": v(293.56, 1.3) * mm, "end": v(306.44, 1.3) * mm, "construction": true});
            skLineSegment(sketch, "E25.3.12.0", {"start": v(294, -3.5) * mm, "end": v(294, -0.03) * mm});
            skLineSegment(sketch, "E25.6.12.0", {"start": v(306, -3.5) * mm, "end": v(306, -0.03) * mm});
            skLineSegment(sketch, "E25.9.12.0", {"start": v(305.5, -4) * mm, "end": v(294.5, -4) * mm});
            skLineSegment(sketch, "E25.12.12.0", {"start": v(305.5, 4) * mm, "end": v(294.5, 4) * mm});
            skPoint(sketch, "E25.15.12.0", {"position": v(300, 0) * mm});
            skPoint(sketch, "E25.16.12.0", {"position": v(294, -4) * mm});
            skPoint(sketch, "E25.17.12.0", {"position": v(294, 4) * mm});
            skPoint(sketch, "E25.18.12.0", {"position": v(306, 4) * mm});
            skPoint(sketch, "E25.19.12.0", {"position": v(306, -4) * mm});
            skPoint(sketch, "E25.20.12.0", {"position": v(300, 0) * mm});
            skLineSegment(sketch, "E25.21.12.0", {"start": v(306, -3.5) * mm, "end": v(305.5, -4) * mm});
            skLineSegment(sketch, "E25.24.12.0", {"start": v(306, 3.5) * mm, "end": v(305.5, 4) * mm});
            skLineSegment(sketch, "E25.27.12.0", {"start": v(294, -3.5) * mm, "end": v(294.5, -4) * mm});
            skLineSegment(sketch, "E25.30.12.0", {"start": v(295.55, 1.85) * mm, "end": v(294.85, 1.85) * mm});
            skLineSegment(sketch, "E25.33.12.0", {"start": v(294, 2.63) * mm, "end": v(294, 3.5) * mm});
            skLineSegment(sketch, "E25.36.12.0", {"start": v(306, 2.63) * mm, "end": v(306, 3.5) * mm});
            skArc(sketch, "E25.39.12.0", {"start": v(305.15, 0.75) * mm, "mid": v(305.5, 0.27) * mm, "end": v(306, -0.03) * mm});
            skLineSegment(sketch, "E25.43.12.0", {"start": v(295.55, 1.85) * mm, "end": v(295.55, 0.75) * mm});
            skLineSegment(sketch, "E25.46.12.0", {"start": v(304.45, 0.75) * mm, "end": v(305.15, 0.75) * mm});
            skLineSegment(sketch, "E25.49.12.0", {"start": v(295.55, 0.75) * mm, "end": v(294.85, 0.75) * mm});
            skArc(sketch, "E25.52.12.0", {"start": v(294, -0.03) * mm, "mid": v(294.5, 0.27) * mm, "end": v(294.85, 0.75) * mm});
            skLineSegment(sketch, "E25.56.12.0", {"start": v(294, 3.5) * mm, "end": v(294.5, 4) * mm});
            skArc(sketch, "E25.59.12.0", {"start": v(294.85, 1.85) * mm, "mid": v(294.5, 2.33) * mm, "end": v(294, 2.63) * mm});
            skLineSegment(sketch, "E25.63.12.0", {"start": v(304.45, 1.85) * mm, "end": v(305.15, 1.85) * mm});
            skArc(sketch, "E25.66.12.0", {"start": v(306, 2.63) * mm, "mid": v(305.5, 2.33) * mm, "end": v(305.15, 1.85) * mm});
            skArc(sketch, "E25.70.12.0", {"start": v(305.15, 0.75) * mm, "mid": v(305.5, 0.27) * mm, "end": v(306, -0.03) * mm});
            skLineSegment(sketch, "E25.74.12.0", {"start": v(304.45, 1.85) * mm, "end": v(304.45, 0.75) * mm});
            skLineSegment(sketch, "E25.0.13.0", {"start": v(318.56, 1.3) * mm, "end": v(331.44, 1.3) * mm, "construction": true});
            skLineSegment(sketch, "E25.3.13.0", {"start": v(319, -3.5) * mm, "end": v(319, -0.03) * mm});
            skLineSegment(sketch, "E25.6.13.0", {"start": v(331, -3.5) * mm, "end": v(331, -0.03) * mm});
            skLineSegment(sketch, "E25.9.13.0", {"start": v(330.5, -4) * mm, "end": v(319.5, -4) * mm});
            skLineSegment(sketch, "E25.12.13.0", {"start": v(330.5, 4) * mm, "end": v(319.5, 4) * mm});
            skPoint(sketch, "E25.15.13.0", {"position": v(325, 0) * mm});
            skPoint(sketch, "E25.16.13.0", {"position": v(319, -4) * mm});
            skPoint(sketch, "E25.17.13.0", {"position": v(319, 4) * mm});
            skPoint(sketch, "E25.18.13.0", {"position": v(331, 4) * mm});
            skPoint(sketch, "E25.19.13.0", {"position": v(331, -4) * mm});
            skPoint(sketch, "E25.20.13.0", {"position": v(325, 0) * mm});
            skLineSegment(sketch, "E25.21.13.0", {"start": v(331, -3.5) * mm, "end": v(330.5, -4) * mm});
            skLineSegment(sketch, "E25.24.13.0", {"start": v(331, 3.5) * mm, "end": v(330.5, 4) * mm});
            skLineSegment(sketch, "E25.27.13.0", {"start": v(319, -3.5) * mm, "end": v(319.5, -4) * mm});
            skLineSegment(sketch, "E25.30.13.0", {"start": v(320.55, 1.85) * mm, "end": v(319.85, 1.85) * mm});
            skLineSegment(sketch, "E25.33.13.0", {"start": v(319, 2.63) * mm, "end": v(319, 3.5) * mm});
            skLineSegment(sketch, "E25.36.13.0", {"start": v(331, 2.63) * mm, "end": v(331, 3.5) * mm});
            skArc(sketch, "E25.39.13.0", {"start": v(330.15, 0.75) * mm, "mid": v(330.5, 0.27) * mm, "end": v(331, -0.03) * mm});
            skLineSegment(sketch, "E25.43.13.0", {"start": v(320.55, 1.85) * mm, "end": v(320.55, 0.75) * mm});
            skLineSegment(sketch, "E25.46.13.0", {"start": v(329.45, 0.75) * mm, "end": v(330.15, 0.75) * mm});
            skLineSegment(sketch, "E25.49.13.0", {"start": v(320.55, 0.75) * mm, "end": v(319.85, 0.75) * mm});
            skArc(sketch, "E25.52.13.0", {"start": v(319, -0.03) * mm, "mid": v(319.5, 0.27) * mm, "end": v(319.85, 0.75) * mm});
            skLineSegment(sketch, "E25.56.13.0", {"start": v(319, 3.5) * mm, "end": v(319.5, 4) * mm});
            skArc(sketch, "E25.59.13.0", {"start": v(319.85, 1.85) * mm, "mid": v(319.5, 2.33) * mm, "end": v(319, 2.63) * mm});
            skLineSegment(sketch, "E25.63.13.0", {"start": v(329.45, 1.85) * mm, "end": v(330.15, 1.85) * mm});
            skArc(sketch, "E25.66.13.0", {"start": v(331, 2.63) * mm, "mid": v(330.5, 2.33) * mm, "end": v(330.15, 1.85) * mm});
            skArc(sketch, "E25.70.13.0", {"start": v(330.15, 0.75) * mm, "mid": v(330.5, 0.27) * mm, "end": v(331, -0.03) * mm});
            skLineSegment(sketch, "E25.74.13.0", {"start": v(329.45, 1.85) * mm, "end": v(329.45, 0.75) * mm});
            skLineSegment(sketch, "E25.0.14.0", {"start": v(343.56, 1.3) * mm, "end": v(356.44, 1.3) * mm, "construction": true});
            skLineSegment(sketch, "E25.3.14.0", {"start": v(344, -3.5) * mm, "end": v(344, -0.03) * mm});
            skLineSegment(sketch, "E25.6.14.0", {"start": v(356, -3.5) * mm, "end": v(356, -0.03) * mm});
            skLineSegment(sketch, "E25.9.14.0", {"start": v(355.5, -4) * mm, "end": v(344.5, -4) * mm});
            skLineSegment(sketch, "E25.12.14.0", {"start": v(355.5, 4) * mm, "end": v(344.5, 4) * mm});
            skPoint(sketch, "E25.15.14.0", {"position": v(350, 0) * mm});
            skPoint(sketch, "E25.16.14.0", {"position": v(344, -4) * mm});
            skPoint(sketch, "E25.17.14.0", {"position": v(344, 4) * mm});
            skPoint(sketch, "E25.18.14.0", {"position": v(356, 4) * mm});
            skPoint(sketch, "E25.19.14.0", {"position": v(356, -4) * mm});
            skPoint(sketch, "E25.20.14.0", {"position": v(350, 0) * mm});
            skLineSegment(sketch, "E25.21.14.0", {"start": v(356, -3.5) * mm, "end": v(355.5, -4) * mm});
            skLineSegment(sketch, "E25.24.14.0", {"start": v(356, 3.5) * mm, "end": v(355.5, 4) * mm});
            skLineSegment(sketch, "E25.27.14.0", {"start": v(344, -3.5) * mm, "end": v(344.5, -4) * mm});
            skLineSegment(sketch, "E25.30.14.0", {"start": v(345.55, 1.85) * mm, "end": v(344.85, 1.85) * mm});
            skLineSegment(sketch, "E25.33.14.0", {"start": v(344, 2.63) * mm, "end": v(344, 3.5) * mm});
            skLineSegment(sketch, "E25.36.14.0", {"start": v(356, 2.63) * mm, "end": v(356, 3.5) * mm});
            skArc(sketch, "E25.39.14.0", {"start": v(355.15, 0.75) * mm, "mid": v(355.5, 0.27) * mm, "end": v(356, -0.03) * mm});
            skLineSegment(sketch, "E25.43.14.0", {"start": v(345.55, 1.85) * mm, "end": v(345.55, 0.75) * mm});
            skLineSegment(sketch, "E25.46.14.0", {"start": v(354.45, 0.75) * mm, "end": v(355.15, 0.75) * mm});
            skLineSegment(sketch, "E25.49.14.0", {"start": v(345.55, 0.75) * mm, "end": v(344.85, 0.75) * mm});
            skArc(sketch, "E25.52.14.0", {"start": v(344, -0.03) * mm, "mid": v(344.5, 0.27) * mm, "end": v(344.85, 0.75) * mm});
            skLineSegment(sketch, "E25.56.14.0", {"start": v(344, 3.5) * mm, "end": v(344.5, 4) * mm});
            skArc(sketch, "E25.59.14.0", {"start": v(344.85, 1.85) * mm, "mid": v(344.5, 2.33) * mm, "end": v(344, 2.63) * mm});
            skLineSegment(sketch, "E25.63.14.0", {"start": v(354.45, 1.85) * mm, "end": v(355.15, 1.85) * mm});
            skArc(sketch, "E25.66.14.0", {"start": v(356, 2.63) * mm, "mid": v(355.5, 2.33) * mm, "end": v(355.15, 1.85) * mm});
            skArc(sketch, "E25.70.14.0", {"start": v(355.15, 0.75) * mm, "mid": v(355.5, 0.27) * mm, "end": v(356, -0.03) * mm});
            skLineSegment(sketch, "E25.74.14.0", {"start": v(354.45, 1.85) * mm, "end": v(354.45, 0.75) * mm});
            skSolve(sketch);
        }
        {
            var Q0;
            Q0=makeQuery(id+"F0.imprint","IMPRINT",FACE,{"disambiguationData":[TD([[makeQuery(id+"F0.imprint","IMPRINT",EDGE,{"derivedFrom":sQuery(id+"F0.wireOp",EDGE,"E1.bottom")}),-1.0]])]});
            extrude(context, id + "F1", {"entities" : qUnion([Q0]), "depth" : 70 * mm, "offsetDistance" : 25 * mm});
        }
        {
            var Q0;
            Q0=makeQuery(id+"F0.imprint","IMPRINT",FACE,{"disambiguationData":[TD([[makeQuery(id+"F0.imprint","IMPRINT",EDGE,{"derivedFrom":sQuery(id+"F0.wireOp",EDGE,"E23.1.0.1")}),-1.0]])]});
            extrude(context, id + "F2", {"entities" : qUnion([Q0]), "depth" : 95 * mm, "offsetDistance" : 25 * mm});
        }
        {
            var Q0;
            Q0=makeQuery(id+"F0.imprint","IMPRINT",FACE,{"disambiguationData":[TD([[makeQuery(id+"F0.imprint","IMPRINT",EDGE,{"derivedFrom":sQuery(id+"F0.wireOp",EDGE,"E23.2.0.1")}),-1.0]])]});
            extrude(context, id + "F3", {"entities" : qUnion([Q0]), "depth" : 120 * mm, "offsetDistance" : 25 * mm});
        }
        {
            var Q0;
            Q0=makeQuery(id+"F0.imprint","IMPRINT",FACE,{"disambiguationData":[TD([[makeQuery(id+"F0.imprint","IMPRINT",EDGE,{"derivedFrom":sQuery(id+"F0.wireOp",EDGE,"E23.3.0.1")}),-1.0]])]});
            extrude(context, id + "F4", {"entities" : qUnion([Q0]), "depth" : 145 * mm, "offsetDistance" : 25 * mm});
        }
        {
            var Q0;
            Q0=makeQuery(id+"F0.imprint","IMPRINT",FACE,{"disambiguationData":[TD([[makeQuery(id+"F0.imprint","IMPRINT",EDGE,{"derivedFrom":sQuery(id+"F0.wireOp",EDGE,"E23.4.0.1")}),-1.0]])]});
            extrude(context, id + "F5", {"entities" : qUnion([Q0]), "depth" : 170 * mm, "offsetDistance" : 25 * mm});
        }
        {
            var Q0;
            Q0=makeQuery(id+"F0.imprint","IMPRINT",FACE,{"disambiguationData":[TD([[makeQuery(id+"F0.imprint","IMPRINT",EDGE,{"derivedFrom":sQuery(id+"F0.wireOp",EDGE,"E23.5.0.1")}),-1.0]])]});
            extrude(context, id + "F6", {"entities" : qUnion([Q0]), "depth" : 195 * mm, "offsetDistance" : 25 * mm});
        }
        {
            var Q0;
            Q0=makeQuery(id+"F0.imprint","IMPRINT",FACE,{"disambiguationData":[TD([[makeQuery(id+"F0.imprint","IMPRINT",EDGE,{"derivedFrom":sQuery(id+"F0.wireOp",EDGE,"E23.6.0.1")}),-1.0]])]});
            extrude(context, id + "F7", {"entities" : qUnion([Q0]), "depth" : 220 * mm, "offsetDistance" : 25 * mm});
        }
        {
            var Q0;
            Q0=makeQuery(id+"F0.imprint","IMPRINT",FACE,{"disambiguationData":[TD([[makeQuery(id+"F0.imprint","IMPRINT",EDGE,{"derivedFrom":sQuery(id+"F0.wireOp",EDGE,"E24.3.7.0")}),-1.0]])]});
            extrude(context, id + "F8", {"entities" : qUnion([Q0]), "depth" : 245 * mm, "offsetDistance" : 25 * mm});
        }
        {
            var Q0;
            Q0=makeQuery(id+"F0.imprint","IMPRINT",FACE,{"disambiguationData":[TD([[makeQuery(id+"F0.imprint","IMPRINT",EDGE,{"derivedFrom":sQuery(id+"F0.wireOp",EDGE,"E24.3.8.0")}),-1.0]])]});
            extrude(context, id + "F9", {"entities" : qUnion([Q0]), "depth" : 270 * mm, "offsetDistance" : 25 * mm});
        }
        {
            var Q0;
            Q0=makeQuery(id+"F0.imprint","IMPRINT",FACE,{"disambiguationData":[TD([[makeQuery(id+"F0.imprint","IMPRINT",EDGE,{"derivedFrom":sQuery(id+"F0.wireOp",EDGE,"E24.3.9.0")}),-1.0]])]});
            extrude(context, id + "F10", {"entities" : qUnion([Q0]), "depth" : 320 * mm, "offsetDistance" : 25 * mm});
        }
        {
            var Q0;
            Q0=makeQuery(id+"F0.imprint","IMPRINT",FACE,{"disambiguationData":[TD([[makeQuery(id+"F0.imprint","IMPRINT",EDGE,{"derivedFrom":sQuery(id+"F0.wireOp",EDGE,"E24.3.10.0")}),-1.0]])]});
            extrude(context, id + "F11", {"entities" : qUnion([Q0]), "depth" : 370 * mm, "offsetDistance" : 25 * mm});
        }
        {
            var Q0;
            Q0=makeQuery(id+"F0.imprint","IMPRINT",FACE,{"disambiguationData":[TD([[makeQuery(id+"F0.imprint","IMPRINT",EDGE,{"derivedFrom":sQuery(id+"F0.wireOp",EDGE,"E25.3.11.0")}),-1.0]])]});
            extrude(context, id + "F12", {"entities" : qUnion([Q0]), "depth" : 470 * mm, "offsetDistance" : 25 * mm});
        }
        {
            var Q0;
            Q0=makeQuery(id+"F0.imprint","IMPRINT",FACE,{"disambiguationData":[TD([[makeQuery(id+"F0.imprint","IMPRINT",EDGE,{"derivedFrom":sQuery(id+"F0.wireOp",EDGE,"E25.3.12.0")}),-1.0]])]});
            extrude(context, id + "F13", {"entities" : qUnion([Q0]), "depth" : 570 * mm, "offsetDistance" : 25 * mm});
        }
        {
            var Q0;
            Q0=makeQuery(id+"F0.imprint","IMPRINT",FACE,{"disambiguationData":[TD([[makeQuery(id+"F0.imprint","IMPRINT",EDGE,{"derivedFrom":sQuery(id+"F0.wireOp",EDGE,"E25.3.13.0")}),-1.0]])]});
            extrude(context, id + "F14", {"entities" : qUnion([Q0]), "depth" : 695 * mm, "offsetDistance" : 25 * mm});
        }
        {
            var Q0;
            Q0=makeQuery(id+"F0.imprint","IMPRINT",FACE,{"disambiguationData":[TD([[makeQuery(id+"F0.imprint","IMPRINT",EDGE,{"derivedFrom":sQuery(id+"F0.wireOp",EDGE,"E25.3.14.0")}),-1.0]])]});
            extrude(context, id + "F15", {"entities" : qUnion([Q0]), "depth" : 1995 * mm, "offsetDistance" : 25 * mm});
        }
        {
            var Q0;
            Q0=makeQuery(id+"F1.opExtrude","SWEPT_FACE",FACE,{"disambiguationData":[OSD([sQuery(id+"F0.wireOp",EDGE,"E1.top")])]});
            var sketch = newSketch(context, id + "F16", { "sketchPlane" : qUnion([Q0])});
            skPoint(sketch, "E26", {"position": v(0, -10) * mm});
            skPoint(sketch, "E27.1.0.0", {"position": v(25, -10) * mm});
            skPoint(sketch, "E27.2.0.0", {"position": v(50, -10) * mm});
            skPoint(sketch, "E27.3.0.0", {"position": v(75, -10) * mm});
            skPoint(sketch, "E27.4.0.0", {"position": v(100, -10) * mm});
            skPoint(sketch, "E27.5.0.0", {"position": v(125, -10) * mm});
            skPoint(sketch, "E27.6.0.0", {"position": v(150, -10) * mm});
            skLineSegment(sketch, "E27.direction1", {"start": v(0, -10) * mm, "end": v(25, -10) * mm, "construction": true});
            skPoint(sketch, "E28.1.0.0", {"position": v(0, -35) * mm});
            skPoint(sketch, "E28.1.0.1", {"position": v(25, -35) * mm});
            skPoint(sketch, "E28.1.0.2", {"position": v(50, -35) * mm});
            skPoint(sketch, "E28.1.0.3", {"position": v(75, -35) * mm});
            skPoint(sketch, "E28.1.0.4", {"position": v(100, -35) * mm});
            skPoint(sketch, "E28.1.0.5", {"position": v(125, -35) * mm});
            skPoint(sketch, "E28.1.0.6", {"position": v(150, -35) * mm});
            skPoint(sketch, "E28.2.0.0", {"position": v(0, -60) * mm});
            skPoint(sketch, "E28.2.0.1", {"position": v(25, -60) * mm});
            skPoint(sketch, "E28.2.0.2", {"position": v(50, -60) * mm});
            skPoint(sketch, "E28.2.0.3", {"position": v(75, -60) * mm});
            skPoint(sketch, "E28.2.0.4", {"position": v(100, -60) * mm});
            skPoint(sketch, "E28.2.0.5", {"position": v(125, -60) * mm});
            skPoint(sketch, "E28.2.0.6", {"position": v(150, -60) * mm});
            skPoint(sketch, "E28.3.0.0", {"position": v(0, -85) * mm});
            skPoint(sketch, "E28.3.0.1", {"position": v(25, -85) * mm});
            skPoint(sketch, "E28.3.0.2", {"position": v(50, -85) * mm});
            skPoint(sketch, "E28.3.0.3", {"position": v(75, -85) * mm});
            skPoint(sketch, "E28.3.0.4", {"position": v(100, -85) * mm});
            skPoint(sketch, "E28.3.0.5", {"position": v(125, -85) * mm});
            skPoint(sketch, "E28.3.0.6", {"position": v(150, -85) * mm});
            skPoint(sketch, "E28.4.0.0", {"position": v(0, -110) * mm});
            skPoint(sketch, "E28.4.0.1", {"position": v(25, -110) * mm});
            skPoint(sketch, "E28.4.0.2", {"position": v(50, -110) * mm});
            skPoint(sketch, "E28.4.0.3", {"position": v(75, -110) * mm});
            skPoint(sketch, "E28.4.0.4", {"position": v(100, -110) * mm});
            skPoint(sketch, "E28.4.0.5", {"position": v(125, -110) * mm});
            skPoint(sketch, "E28.4.0.6", {"position": v(150, -110) * mm});
            skPoint(sketch, "E28.5.0.0", {"position": v(0, -135) * mm});
            skPoint(sketch, "E28.5.0.1", {"position": v(25, -135) * mm});
            skPoint(sketch, "E28.5.0.2", {"position": v(50, -135) * mm});
            skPoint(sketch, "E28.5.0.3", {"position": v(75, -135) * mm});
            skPoint(sketch, "E28.5.0.4", {"position": v(100, -135) * mm});
            skPoint(sketch, "E28.5.0.5", {"position": v(125, -135) * mm});
            skPoint(sketch, "E28.5.0.6", {"position": v(150, -135) * mm});
            skPoint(sketch, "E28.6.0.0", {"position": v(0, -160) * mm});
            skPoint(sketch, "E28.6.0.1", {"position": v(25, -160) * mm});
            skPoint(sketch, "E28.6.0.2", {"position": v(50, -160) * mm});
            skPoint(sketch, "E28.6.0.3", {"position": v(75, -160) * mm});
            skPoint(sketch, "E28.6.0.4", {"position": v(100, -160) * mm});
            skPoint(sketch, "E28.6.0.5", {"position": v(125, -160) * mm});
            skPoint(sketch, "E28.6.0.6", {"position": v(150, -160) * mm});
            skPoint(sketch, "E28.7.0.0", {"position": v(0, -185) * mm});
            skPoint(sketch, "E28.7.0.1", {"position": v(25, -185) * mm});
            skPoint(sketch, "E28.7.0.2", {"position": v(50, -185) * mm});
            skPoint(sketch, "E28.7.0.3", {"position": v(75, -185) * mm});
            skPoint(sketch, "E28.7.0.4", {"position": v(100, -185) * mm});
            skPoint(sketch, "E28.7.0.5", {"position": v(125, -185) * mm});
            skPoint(sketch, "E28.7.0.6", {"position": v(150, -185) * mm});
            skPoint(sketch, "E28.8.0.0", {"position": v(0, -210) * mm});
            skPoint(sketch, "E28.8.0.1", {"position": v(25, -210) * mm});
            skPoint(sketch, "E28.8.0.2", {"position": v(50, -210) * mm});
            skPoint(sketch, "E28.8.0.3", {"position": v(75, -210) * mm});
            skPoint(sketch, "E28.8.0.4", {"position": v(100, -210) * mm});
            skPoint(sketch, "E28.8.0.5", {"position": v(125, -210) * mm});
            skPoint(sketch, "E28.8.0.6", {"position": v(150, -210) * mm});
            skLineSegment(sketch, "E28.direction1", {"start": v(0, -10) * mm, "end": v(0, -35) * mm, "construction": true});
            skPoint(sketch, "E29.0.7.0", {"position": v(175, -10) * mm});
            skPoint(sketch, "E29.0.8.0", {"position": v(200, -10) * mm});
            skPoint(sketch, "E29.0.9.0", {"position": v(225, -10) * mm});
            skPoint(sketch, "E29.0.10.0", {"position": v(250, -10) * mm});
            skPoint(sketch, "E30.1.0.0", {"position": v(250, -35) * mm});
            skPoint(sketch, "E30.1.0.1", {"position": v(225, -35) * mm});
            skPoint(sketch, "E30.1.0.2", {"position": v(200, -35) * mm});
            skPoint(sketch, "E30.1.0.3", {"position": v(175, -35) * mm});
            skPoint(sketch, "E30.2.0.0", {"position": v(250, -60) * mm});
            skPoint(sketch, "E30.2.0.1", {"position": v(225, -60) * mm});
            skPoint(sketch, "E30.2.0.2", {"position": v(200, -60) * mm});
            skPoint(sketch, "E30.2.0.3", {"position": v(175, -60) * mm});
            skLineSegment(sketch, "E30.direction1", {"start": v(175, -10) * mm, "end": v(175, -35) * mm, "construction": true});
            skPoint(sketch, "E31.0.3.0", {"position": v(250, -85) * mm});
            skPoint(sketch, "E31.1.3.0", {"position": v(225, -85) * mm});
            skPoint(sketch, "E31.2.3.0", {"position": v(200, -85) * mm});
            skPoint(sketch, "E31.3.3.0", {"position": v(175, -85) * mm});
            skPoint(sketch, "E31.0.4.0", {"position": v(250, -110) * mm});
            skPoint(sketch, "E31.1.4.0", {"position": v(225, -110) * mm});
            skPoint(sketch, "E31.2.4.0", {"position": v(200, -110) * mm});
            skPoint(sketch, "E31.3.4.0", {"position": v(175, -110) * mm});
            skPoint(sketch, "E31.0.5.0", {"position": v(250, -135) * mm});
            skPoint(sketch, "E31.1.5.0", {"position": v(225, -135) * mm});
            skPoint(sketch, "E31.2.5.0", {"position": v(200, -135) * mm});
            skPoint(sketch, "E31.3.5.0", {"position": v(175, -135) * mm});
            skPoint(sketch, "E31.0.6.0", {"position": v(250, -160) * mm});
            skPoint(sketch, "E31.1.6.0", {"position": v(225, -160) * mm});
            skPoint(sketch, "E31.2.6.0", {"position": v(200, -160) * mm});
            skPoint(sketch, "E31.3.6.0", {"position": v(175, -160) * mm});
            skPoint(sketch, "E31.0.7.0", {"position": v(250, -185) * mm});
            skPoint(sketch, "E31.1.7.0", {"position": v(225, -185) * mm});
            skPoint(sketch, "E31.2.7.0", {"position": v(200, -185) * mm});
            skPoint(sketch, "E31.3.7.0", {"position": v(175, -185) * mm});
            skPoint(sketch, "E31.0.8.0", {"position": v(250, -210) * mm});
            skPoint(sketch, "E31.1.8.0", {"position": v(225, -210) * mm});
            skPoint(sketch, "E31.2.8.0", {"position": v(200, -210) * mm});
            skPoint(sketch, "E31.3.8.0", {"position": v(175, -210) * mm});
            skPoint(sketch, "E31.0.9.0", {"position": v(250, -235) * mm});
            skPoint(sketch, "E31.1.9.0", {"position": v(225, -235) * mm});
            skPoint(sketch, "E31.2.9.0", {"position": v(200, -235) * mm});
            skPoint(sketch, "E31.3.9.0", {"position": v(175, -235) * mm});
            skPoint(sketch, "E31.0.10.0", {"position": v(250, -260) * mm});
            skPoint(sketch, "E31.1.10.0", {"position": v(225, -260) * mm});
            skPoint(sketch, "E31.2.10.0", {"position": v(200, -260) * mm});
            skPoint(sketch, "E31.3.10.0", {"position": v(175, -260) * mm});
            skPoint(sketch, "E31.0.11.0", {"position": v(250, -285) * mm});
            skPoint(sketch, "E31.1.11.0", {"position": v(225, -285) * mm});
            skPoint(sketch, "E31.2.11.0", {"position": v(200, -285) * mm});
            skPoint(sketch, "E31.3.11.0", {"position": v(175, -285) * mm});
            skPoint(sketch, "E31.0.12.0", {"position": v(250, -310) * mm});
            skPoint(sketch, "E31.1.12.0", {"position": v(225, -310) * mm});
            skPoint(sketch, "E31.2.12.0", {"position": v(200, -310) * mm});
            skPoint(sketch, "E31.3.12.0", {"position": v(175, -310) * mm});
            skPoint(sketch, "E31.0.13.0", {"position": v(250, -335) * mm});
            skPoint(sketch, "E31.1.13.0", {"position": v(225, -335) * mm});
            skPoint(sketch, "E31.2.13.0", {"position": v(200, -335) * mm});
            skPoint(sketch, "E31.3.13.0", {"position": v(175, -335) * mm});
            skPoint(sketch, "E31.0.14.0", {"position": v(250, -360) * mm});
            skPoint(sketch, "E31.1.14.0", {"position": v(225, -360) * mm});
            skPoint(sketch, "E31.2.14.0", {"position": v(200, -360) * mm});
            skPoint(sketch, "E31.3.14.0", {"position": v(175, -360) * mm});
            skPoint(sketch, "E32.0.11.0", {"position": v(275, -10) * mm});
            skPoint(sketch, "E32.0.12.0", {"position": v(300, -10) * mm});
            skPoint(sketch, "E32.0.13.0", {"position": v(325, -10) * mm});
            skPoint(sketch, "E32.0.14.0", {"position": v(350, -10) * mm});
            skPoint(sketch, "E33.1.0.0", {"position": v(350, -35) * mm});
            skPoint(sketch, "E33.1.0.1", {"position": v(275, -35) * mm});
            skPoint(sketch, "E33.1.0.2", {"position": v(325, -35) * mm});
            skPoint(sketch, "E33.1.0.3", {"position": v(300, -35) * mm});
            skPoint(sketch, "E33.2.0.0", {"position": v(350, -60) * mm});
            skPoint(sketch, "E33.2.0.1", {"position": v(275, -60) * mm});
            skPoint(sketch, "E33.2.0.2", {"position": v(325, -60) * mm});
            skPoint(sketch, "E33.2.0.3", {"position": v(300, -60) * mm});
            skLineSegment(sketch, "E33.direction1", {"start": v(275, -10) * mm, "end": v(275, -35) * mm, "construction": true});
            skPoint(sketch, "E34.0.3.0", {"position": v(350, -85) * mm});
            skPoint(sketch, "E34.1.3.0", {"position": v(275, -85) * mm});
            skPoint(sketch, "E34.2.3.0", {"position": v(325, -85) * mm});
            skPoint(sketch, "E34.3.3.0", {"position": v(300, -85) * mm});
            skPoint(sketch, "E34.0.4.0", {"position": v(350, -110) * mm});
            skPoint(sketch, "E34.1.4.0", {"position": v(275, -110) * mm});
            skPoint(sketch, "E34.2.4.0", {"position": v(325, -110) * mm});
            skPoint(sketch, "E34.3.4.0", {"position": v(300, -110) * mm});
            skPoint(sketch, "E34.0.5.0", {"position": v(350, -135) * mm});
            skPoint(sketch, "E34.1.5.0", {"position": v(275, -135) * mm});
            skPoint(sketch, "E34.2.5.0", {"position": v(325, -135) * mm});
            skPoint(sketch, "E34.3.5.0", {"position": v(300, -135) * mm});
            skPoint(sketch, "E34.0.6.0", {"position": v(350, -160) * mm});
            skPoint(sketch, "E34.1.6.0", {"position": v(275, -160) * mm});
            skPoint(sketch, "E34.2.6.0", {"position": v(325, -160) * mm});
            skPoint(sketch, "E34.3.6.0", {"position": v(300, -160) * mm});
            skPoint(sketch, "E34.0.7.0", {"position": v(350, -185) * mm});
            skPoint(sketch, "E34.1.7.0", {"position": v(275, -185) * mm});
            skPoint(sketch, "E34.2.7.0", {"position": v(325, -185) * mm});
            skPoint(sketch, "E34.3.7.0", {"position": v(300, -185) * mm});
            skPoint(sketch, "E34.0.8.0", {"position": v(350, -210) * mm});
            skPoint(sketch, "E34.1.8.0", {"position": v(275, -210) * mm});
            skPoint(sketch, "E34.2.8.0", {"position": v(325, -210) * mm});
            skPoint(sketch, "E34.3.8.0", {"position": v(300, -210) * mm});
            skPoint(sketch, "E34.0.9.0", {"position": v(350, -235) * mm});
            skPoint(sketch, "E34.1.9.0", {"position": v(275, -235) * mm});
            skPoint(sketch, "E34.2.9.0", {"position": v(325, -235) * mm});
            skPoint(sketch, "E34.3.9.0", {"position": v(300, -235) * mm});
            skPoint(sketch, "E34.0.10.0", {"position": v(350, -260) * mm});
            skPoint(sketch, "E34.1.10.0", {"position": v(275, -260) * mm});
            skPoint(sketch, "E34.2.10.0", {"position": v(325, -260) * mm});
            skPoint(sketch, "E34.3.10.0", {"position": v(300, -260) * mm});
            skPoint(sketch, "E34.0.11.0", {"position": v(350, -285) * mm});
            skPoint(sketch, "E34.1.11.0", {"position": v(275, -285) * mm});
            skPoint(sketch, "E34.2.11.0", {"position": v(325, -285) * mm});
            skPoint(sketch, "E34.3.11.0", {"position": v(300, -285) * mm});
            skPoint(sketch, "E34.0.12.0", {"position": v(350, -310) * mm});
            skPoint(sketch, "E34.1.12.0", {"position": v(275, -310) * mm});
            skPoint(sketch, "E34.2.12.0", {"position": v(325, -310) * mm});
            skPoint(sketch, "E34.3.12.0", {"position": v(300, -310) * mm});
            skPoint(sketch, "E34.0.13.0", {"position": v(350, -335) * mm});
            skPoint(sketch, "E34.1.13.0", {"position": v(275, -335) * mm});
            skPoint(sketch, "E34.2.13.0", {"position": v(325, -335) * mm});
            skPoint(sketch, "E34.3.13.0", {"position": v(300, -335) * mm});
            skPoint(sketch, "E34.0.14.0", {"position": v(350, -360) * mm});
            skPoint(sketch, "E34.1.14.0", {"position": v(275, -360) * mm});
            skPoint(sketch, "E34.2.14.0", {"position": v(325, -360) * mm});
            skPoint(sketch, "E34.3.14.0", {"position": v(300, -360) * mm});
            skPoint(sketch, "E34.0.15.0", {"position": v(350, -385) * mm});
            skPoint(sketch, "E34.1.15.0", {"position": v(275, -385) * mm});
            skPoint(sketch, "E34.2.15.0", {"position": v(325, -385) * mm});
            skPoint(sketch, "E34.3.15.0", {"position": v(300, -385) * mm});
            skPoint(sketch, "E34.0.16.0", {"position": v(350, -410) * mm});
            skPoint(sketch, "E34.1.16.0", {"position": v(275, -410) * mm});
            skPoint(sketch, "E34.2.16.0", {"position": v(325, -410) * mm});
            skPoint(sketch, "E34.3.16.0", {"position": v(300, -410) * mm});
            skPoint(sketch, "E34.0.17.0", {"position": v(350, -435) * mm});
            skPoint(sketch, "E34.1.17.0", {"position": v(275, -435) * mm});
            skPoint(sketch, "E34.2.17.0", {"position": v(325, -435) * mm});
            skPoint(sketch, "E34.3.17.0", {"position": v(300, -435) * mm});
            skPoint(sketch, "E34.0.18.0", {"position": v(350, -460) * mm});
            skPoint(sketch, "E34.1.18.0", {"position": v(275, -460) * mm});
            skPoint(sketch, "E34.2.18.0", {"position": v(325, -460) * mm});
            skPoint(sketch, "E34.3.18.0", {"position": v(300, -460) * mm});
            skPoint(sketch, "E34.0.19.0", {"position": v(350, -485) * mm});
            skPoint(sketch, "E34.1.19.0", {"position": v(275, -485) * mm});
            skPoint(sketch, "E34.2.19.0", {"position": v(325, -485) * mm});
            skPoint(sketch, "E34.3.19.0", {"position": v(300, -485) * mm});
            skPoint(sketch, "E34.0.20.0", {"position": v(350, -510) * mm});
            skPoint(sketch, "E34.1.20.0", {"position": v(275, -510) * mm});
            skPoint(sketch, "E34.2.20.0", {"position": v(325, -510) * mm});
            skPoint(sketch, "E34.3.20.0", {"position": v(300, -510) * mm});
            skPoint(sketch, "E34.0.21.0", {"position": v(350, -535) * mm});
            skPoint(sketch, "E34.1.21.0", {"position": v(275, -535) * mm});
            skPoint(sketch, "E34.2.21.0", {"position": v(325, -535) * mm});
            skPoint(sketch, "E34.3.21.0", {"position": v(300, -535) * mm});
            skPoint(sketch, "E34.0.22.0", {"position": v(350, -560) * mm});
            skPoint(sketch, "E34.1.22.0", {"position": v(275, -560) * mm});
            skPoint(sketch, "E34.2.22.0", {"position": v(325, -560) * mm});
            skPoint(sketch, "E34.3.22.0", {"position": v(300, -560) * mm});
            skPoint(sketch, "E34.0.23.0", {"position": v(350, -585) * mm});
            skPoint(sketch, "E34.1.23.0", {"position": v(275, -585) * mm});
            skPoint(sketch, "E34.2.23.0", {"position": v(325, -585) * mm});
            skPoint(sketch, "E34.3.23.0", {"position": v(300, -585) * mm});
            skPoint(sketch, "E34.0.24.0", {"position": v(350, -610) * mm});
            skPoint(sketch, "E34.1.24.0", {"position": v(275, -610) * mm});
            skPoint(sketch, "E34.2.24.0", {"position": v(325, -610) * mm});
            skPoint(sketch, "E34.3.24.0", {"position": v(300, -610) * mm});
            skPoint(sketch, "E34.0.25.0", {"position": v(350, -635) * mm});
            skPoint(sketch, "E34.1.25.0", {"position": v(275, -635) * mm});
            skPoint(sketch, "E34.2.25.0", {"position": v(325, -635) * mm});
            skPoint(sketch, "E34.3.25.0", {"position": v(300, -635) * mm});
            skPoint(sketch, "E34.0.26.0", {"position": v(350, -660) * mm});
            skPoint(sketch, "E34.1.26.0", {"position": v(275, -660) * mm});
            skPoint(sketch, "E34.2.26.0", {"position": v(325, -660) * mm});
            skPoint(sketch, "E34.3.26.0", {"position": v(300, -660) * mm});
            skPoint(sketch, "E34.0.27.0", {"position": v(350, -685) * mm});
            skPoint(sketch, "E34.1.27.0", {"position": v(275, -685) * mm});
            skPoint(sketch, "E34.2.27.0", {"position": v(325, -685) * mm});
            skPoint(sketch, "E34.3.27.0", {"position": v(300, -685) * mm});
            skPoint(sketch, "E34.0.28.0", {"position": v(350, -710) * mm});
            skPoint(sketch, "E34.1.28.0", {"position": v(275, -710) * mm});
            skPoint(sketch, "E34.2.28.0", {"position": v(325, -710) * mm});
            skPoint(sketch, "E34.3.28.0", {"position": v(300, -710) * mm});
            skPoint(sketch, "E34.0.29.0", {"position": v(350, -735) * mm});
            skPoint(sketch, "E34.1.29.0", {"position": v(275, -735) * mm});
            skPoint(sketch, "E34.2.29.0", {"position": v(325, -735) * mm});
            skPoint(sketch, "E34.3.29.0", {"position": v(300, -735) * mm});
            skPoint(sketch, "E34.0.30.0", {"position": v(350, -760) * mm});
            skPoint(sketch, "E34.1.30.0", {"position": v(275, -760) * mm});
            skPoint(sketch, "E34.2.30.0", {"position": v(325, -760) * mm});
            skPoint(sketch, "E34.3.30.0", {"position": v(300, -760) * mm});
            skPoint(sketch, "E34.0.31.0", {"position": v(350, -785) * mm});
            skPoint(sketch, "E34.1.31.0", {"position": v(275, -785) * mm});
            skPoint(sketch, "E34.2.31.0", {"position": v(325, -785) * mm});
            skPoint(sketch, "E34.3.31.0", {"position": v(300, -785) * mm});
            skPoint(sketch, "E34.0.32.0", {"position": v(350, -810) * mm});
            skPoint(sketch, "E34.1.32.0", {"position": v(275, -810) * mm});
            skPoint(sketch, "E34.2.32.0", {"position": v(325, -810) * mm});
            skPoint(sketch, "E34.3.32.0", {"position": v(300, -810) * mm});
            skPoint(sketch, "E34.0.33.0", {"position": v(350, -835) * mm});
            skPoint(sketch, "E34.1.33.0", {"position": v(275, -835) * mm});
            skPoint(sketch, "E34.2.33.0", {"position": v(325, -835) * mm});
            skPoint(sketch, "E34.3.33.0", {"position": v(300, -835) * mm});
            skPoint(sketch, "E34.0.34.0", {"position": v(350, -860) * mm});
            skPoint(sketch, "E34.1.34.0", {"position": v(275, -860) * mm});
            skPoint(sketch, "E34.2.34.0", {"position": v(325, -860) * mm});
            skPoint(sketch, "E34.3.34.0", {"position": v(300, -860) * mm});
            skPoint(sketch, "E34.0.35.0", {"position": v(350, -885) * mm});
            skPoint(sketch, "E34.1.35.0", {"position": v(275, -885) * mm});
            skPoint(sketch, "E34.2.35.0", {"position": v(325, -885) * mm});
            skPoint(sketch, "E34.3.35.0", {"position": v(300, -885) * mm});
            skPoint(sketch, "E34.0.36.0", {"position": v(350, -910) * mm});
            skPoint(sketch, "E34.1.36.0", {"position": v(275, -910) * mm});
            skPoint(sketch, "E34.2.36.0", {"position": v(325, -910) * mm});
            skPoint(sketch, "E34.3.36.0", {"position": v(300, -910) * mm});
            skPoint(sketch, "E34.0.37.0", {"position": v(350, -935) * mm});
            skPoint(sketch, "E34.1.37.0", {"position": v(275, -935) * mm});
            skPoint(sketch, "E34.2.37.0", {"position": v(325, -935) * mm});
            skPoint(sketch, "E34.3.37.0", {"position": v(300, -935) * mm});
            skPoint(sketch, "E34.0.38.0", {"position": v(350, -960) * mm});
            skPoint(sketch, "E34.1.38.0", {"position": v(275, -960) * mm});
            skPoint(sketch, "E34.2.38.0", {"position": v(325, -960) * mm});
            skPoint(sketch, "E34.3.38.0", {"position": v(300, -960) * mm});
            skPoint(sketch, "E34.0.39.0", {"position": v(350, -985) * mm});
            skPoint(sketch, "E34.1.39.0", {"position": v(275, -985) * mm});
            skPoint(sketch, "E34.2.39.0", {"position": v(325, -985) * mm});
            skPoint(sketch, "E34.3.39.0", {"position": v(300, -985) * mm});
            skPoint(sketch, "E34.0.40.0", {"position": v(350, -1010) * mm});
            skPoint(sketch, "E34.1.40.0", {"position": v(275, -1010) * mm});
            skPoint(sketch, "E34.2.40.0", {"position": v(325, -1010) * mm});
            skPoint(sketch, "E34.3.40.0", {"position": v(300, -1010) * mm});
            skPoint(sketch, "E34.0.41.0", {"position": v(350, -1035) * mm});
            skPoint(sketch, "E34.1.41.0", {"position": v(275, -1035) * mm});
            skPoint(sketch, "E34.2.41.0", {"position": v(325, -1035) * mm});
            skPoint(sketch, "E34.3.41.0", {"position": v(300, -1035) * mm});
            skPoint(sketch, "E34.0.42.0", {"position": v(350, -1060) * mm});
            skPoint(sketch, "E34.1.42.0", {"position": v(275, -1060) * mm});
            skPoint(sketch, "E34.2.42.0", {"position": v(325, -1060) * mm});
            skPoint(sketch, "E34.3.42.0", {"position": v(300, -1060) * mm});
            skPoint(sketch, "E34.0.43.0", {"position": v(350, -1085) * mm});
            skPoint(sketch, "E34.1.43.0", {"position": v(275, -1085) * mm});
            skPoint(sketch, "E34.2.43.0", {"position": v(325, -1085) * mm});
            skPoint(sketch, "E34.3.43.0", {"position": v(300, -1085) * mm});
            skPoint(sketch, "E34.0.44.0", {"position": v(350, -1110) * mm});
            skPoint(sketch, "E34.1.44.0", {"position": v(275, -1110) * mm});
            skPoint(sketch, "E34.2.44.0", {"position": v(325, -1110) * mm});
            skPoint(sketch, "E34.3.44.0", {"position": v(300, -1110) * mm});
            skPoint(sketch, "E34.0.45.0", {"position": v(350, -1135) * mm});
            skPoint(sketch, "E34.1.45.0", {"position": v(275, -1135) * mm});
            skPoint(sketch, "E34.2.45.0", {"position": v(325, -1135) * mm});
            skPoint(sketch, "E34.3.45.0", {"position": v(300, -1135) * mm});
            skPoint(sketch, "E34.0.46.0", {"position": v(350, -1160) * mm});
            skPoint(sketch, "E34.1.46.0", {"position": v(275, -1160) * mm});
            skPoint(sketch, "E34.2.46.0", {"position": v(325, -1160) * mm});
            skPoint(sketch, "E34.3.46.0", {"position": v(300, -1160) * mm});
            skPoint(sketch, "E34.0.47.0", {"position": v(350, -1185) * mm});
            skPoint(sketch, "E34.1.47.0", {"position": v(275, -1185) * mm});
            skPoint(sketch, "E34.2.47.0", {"position": v(325, -1185) * mm});
            skPoint(sketch, "E34.3.47.0", {"position": v(300, -1185) * mm});
            skPoint(sketch, "E34.0.48.0", {"position": v(350, -1210) * mm});
            skPoint(sketch, "E34.1.48.0", {"position": v(275, -1210) * mm});
            skPoint(sketch, "E34.2.48.0", {"position": v(325, -1210) * mm});
            skPoint(sketch, "E34.3.48.0", {"position": v(300, -1210) * mm});
            skPoint(sketch, "E34.0.49.0", {"position": v(350, -1235) * mm});
            skPoint(sketch, "E34.1.49.0", {"position": v(275, -1235) * mm});
            skPoint(sketch, "E34.2.49.0", {"position": v(325, -1235) * mm});
            skPoint(sketch, "E34.3.49.0", {"position": v(300, -1235) * mm});
            skPoint(sketch, "E34.0.50.0", {"position": v(350, -1260) * mm});
            skPoint(sketch, "E34.1.50.0", {"position": v(275, -1260) * mm});
            skPoint(sketch, "E34.2.50.0", {"position": v(325, -1260) * mm});
            skPoint(sketch, "E34.3.50.0", {"position": v(300, -1260) * mm});
            skPoint(sketch, "E34.0.51.0", {"position": v(350, -1285) * mm});
            skPoint(sketch, "E34.1.51.0", {"position": v(275, -1285) * mm});
            skPoint(sketch, "E34.2.51.0", {"position": v(325, -1285) * mm});
            skPoint(sketch, "E34.3.51.0", {"position": v(300, -1285) * mm});
            skPoint(sketch, "E34.0.52.0", {"position": v(350, -1310) * mm});
            skPoint(sketch, "E34.1.52.0", {"position": v(275, -1310) * mm});
            skPoint(sketch, "E34.2.52.0", {"position": v(325, -1310) * mm});
            skPoint(sketch, "E34.3.52.0", {"position": v(300, -1310) * mm});
            skPoint(sketch, "E34.0.53.0", {"position": v(350, -1335) * mm});
            skPoint(sketch, "E34.1.53.0", {"position": v(275, -1335) * mm});
            skPoint(sketch, "E34.2.53.0", {"position": v(325, -1335) * mm});
            skPoint(sketch, "E34.3.53.0", {"position": v(300, -1335) * mm});
            skPoint(sketch, "E34.0.54.0", {"position": v(350, -1360) * mm});
            skPoint(sketch, "E34.1.54.0", {"position": v(275, -1360) * mm});
            skPoint(sketch, "E34.2.54.0", {"position": v(325, -1360) * mm});
            skPoint(sketch, "E34.3.54.0", {"position": v(300, -1360) * mm});
            skPoint(sketch, "E34.0.55.0", {"position": v(350, -1385) * mm});
            skPoint(sketch, "E34.1.55.0", {"position": v(275, -1385) * mm});
            skPoint(sketch, "E34.2.55.0", {"position": v(325, -1385) * mm});
            skPoint(sketch, "E34.3.55.0", {"position": v(300, -1385) * mm});
            skPoint(sketch, "E34.0.56.0", {"position": v(350, -1410) * mm});
            skPoint(sketch, "E34.1.56.0", {"position": v(275, -1410) * mm});
            skPoint(sketch, "E34.2.56.0", {"position": v(325, -1410) * mm});
            skPoint(sketch, "E34.3.56.0", {"position": v(300, -1410) * mm});
            skPoint(sketch, "E34.0.57.0", {"position": v(350, -1435) * mm});
            skPoint(sketch, "E34.1.57.0", {"position": v(275, -1435) * mm});
            skPoint(sketch, "E34.2.57.0", {"position": v(325, -1435) * mm});
            skPoint(sketch, "E34.3.57.0", {"position": v(300, -1435) * mm});
            skPoint(sketch, "E34.0.58.0", {"position": v(350, -1460) * mm});
            skPoint(sketch, "E34.1.58.0", {"position": v(275, -1460) * mm});
            skPoint(sketch, "E34.2.58.0", {"position": v(325, -1460) * mm});
            skPoint(sketch, "E34.3.58.0", {"position": v(300, -1460) * mm});
            skPoint(sketch, "E34.0.59.0", {"position": v(350, -1485) * mm});
            skPoint(sketch, "E34.1.59.0", {"position": v(275, -1485) * mm});
            skPoint(sketch, "E34.2.59.0", {"position": v(325, -1485) * mm});
            skPoint(sketch, "E34.3.59.0", {"position": v(300, -1485) * mm});
            skPoint(sketch, "E34.0.60.0", {"position": v(350, -1510) * mm});
            skPoint(sketch, "E34.1.60.0", {"position": v(275, -1510) * mm});
            skPoint(sketch, "E34.2.60.0", {"position": v(325, -1510) * mm});
            skPoint(sketch, "E34.3.60.0", {"position": v(300, -1510) * mm});
            skPoint(sketch, "E34.0.61.0", {"position": v(350, -1535) * mm});
            skPoint(sketch, "E34.1.61.0", {"position": v(275, -1535) * mm});
            skPoint(sketch, "E34.2.61.0", {"position": v(325, -1535) * mm});
            skPoint(sketch, "E34.3.61.0", {"position": v(300, -1535) * mm});
            skPoint(sketch, "E34.0.62.0", {"position": v(350, -1560) * mm});
            skPoint(sketch, "E34.1.62.0", {"position": v(275, -1560) * mm});
            skPoint(sketch, "E34.2.62.0", {"position": v(325, -1560) * mm});
            skPoint(sketch, "E34.3.62.0", {"position": v(300, -1560) * mm});
            skPoint(sketch, "E34.0.63.0", {"position": v(350, -1585) * mm});
            skPoint(sketch, "E34.1.63.0", {"position": v(275, -1585) * mm});
            skPoint(sketch, "E34.2.63.0", {"position": v(325, -1585) * mm});
            skPoint(sketch, "E34.3.63.0", {"position": v(300, -1585) * mm});
            skPoint(sketch, "E34.0.64.0", {"position": v(350, -1610) * mm});
            skPoint(sketch, "E34.1.64.0", {"position": v(275, -1610) * mm});
            skPoint(sketch, "E34.2.64.0", {"position": v(325, -1610) * mm});
            skPoint(sketch, "E34.3.64.0", {"position": v(300, -1610) * mm});
            skPoint(sketch, "E34.0.65.0", {"position": v(350, -1635) * mm});
            skPoint(sketch, "E34.1.65.0", {"position": v(275, -1635) * mm});
            skPoint(sketch, "E34.2.65.0", {"position": v(325, -1635) * mm});
            skPoint(sketch, "E34.3.65.0", {"position": v(300, -1635) * mm});
            skPoint(sketch, "E34.0.66.0", {"position": v(350, -1660) * mm});
            skPoint(sketch, "E34.1.66.0", {"position": v(275, -1660) * mm});
            skPoint(sketch, "E34.2.66.0", {"position": v(325, -1660) * mm});
            skPoint(sketch, "E34.3.66.0", {"position": v(300, -1660) * mm});
            skPoint(sketch, "E34.0.67.0", {"position": v(350, -1685) * mm});
            skPoint(sketch, "E34.1.67.0", {"position": v(275, -1685) * mm});
            skPoint(sketch, "E34.2.67.0", {"position": v(325, -1685) * mm});
            skPoint(sketch, "E34.3.67.0", {"position": v(300, -1685) * mm});
            skPoint(sketch, "E34.0.68.0", {"position": v(350, -1710) * mm});
            skPoint(sketch, "E34.1.68.0", {"position": v(275, -1710) * mm});
            skPoint(sketch, "E34.2.68.0", {"position": v(325, -1710) * mm});
            skPoint(sketch, "E34.3.68.0", {"position": v(300, -1710) * mm});
            skPoint(sketch, "E34.0.69.0", {"position": v(350, -1735) * mm});
            skPoint(sketch, "E34.1.69.0", {"position": v(275, -1735) * mm});
            skPoint(sketch, "E34.2.69.0", {"position": v(325, -1735) * mm});
            skPoint(sketch, "E34.3.69.0", {"position": v(300, -1735) * mm});
            skPoint(sketch, "E34.0.70.0", {"position": v(350, -1760) * mm});
            skPoint(sketch, "E34.1.70.0", {"position": v(275, -1760) * mm});
            skPoint(sketch, "E34.2.70.0", {"position": v(325, -1760) * mm});
            skPoint(sketch, "E34.3.70.0", {"position": v(300, -1760) * mm});
            skPoint(sketch, "E34.0.71.0", {"position": v(350, -1785) * mm});
            skPoint(sketch, "E34.1.71.0", {"position": v(275, -1785) * mm});
            skPoint(sketch, "E34.2.71.0", {"position": v(325, -1785) * mm});
            skPoint(sketch, "E34.3.71.0", {"position": v(300, -1785) * mm});
            skPoint(sketch, "E34.0.72.0", {"position": v(350, -1810) * mm});
            skPoint(sketch, "E34.1.72.0", {"position": v(275, -1810) * mm});
            skPoint(sketch, "E34.2.72.0", {"position": v(325, -1810) * mm});
            skPoint(sketch, "E34.3.72.0", {"position": v(300, -1810) * mm});
            skPoint(sketch, "E34.0.73.0", {"position": v(350, -1835) * mm});
            skPoint(sketch, "E34.1.73.0", {"position": v(275, -1835) * mm});
            skPoint(sketch, "E34.2.73.0", {"position": v(325, -1835) * mm});
            skPoint(sketch, "E34.3.73.0", {"position": v(300, -1835) * mm});
            skPoint(sketch, "E34.0.74.0", {"position": v(350, -1860) * mm});
            skPoint(sketch, "E34.1.74.0", {"position": v(275, -1860) * mm});
            skPoint(sketch, "E34.2.74.0", {"position": v(325, -1860) * mm});
            skPoint(sketch, "E34.3.74.0", {"position": v(300, -1860) * mm});
            skPoint(sketch, "E34.0.75.0", {"position": v(350, -1885) * mm});
            skPoint(sketch, "E34.1.75.0", {"position": v(275, -1885) * mm});
            skPoint(sketch, "E34.2.75.0", {"position": v(325, -1885) * mm});
            skPoint(sketch, "E34.3.75.0", {"position": v(300, -1885) * mm});
            skPoint(sketch, "E34.0.76.0", {"position": v(350, -1910) * mm});
            skPoint(sketch, "E34.1.76.0", {"position": v(275, -1910) * mm});
            skPoint(sketch, "E34.2.76.0", {"position": v(325, -1910) * mm});
            skPoint(sketch, "E34.3.76.0", {"position": v(300, -1910) * mm});
            skPoint(sketch, "E34.0.77.0", {"position": v(350, -1935) * mm});
            skPoint(sketch, "E34.1.77.0", {"position": v(275, -1935) * mm});
            skPoint(sketch, "E34.2.77.0", {"position": v(325, -1935) * mm});
            skPoint(sketch, "E34.3.77.0", {"position": v(300, -1935) * mm});
            skPoint(sketch, "E34.0.78.0", {"position": v(350, -1960) * mm});
            skPoint(sketch, "E34.1.78.0", {"position": v(275, -1960) * mm});
            skPoint(sketch, "E34.2.78.0", {"position": v(325, -1960) * mm});
            skPoint(sketch, "E34.3.78.0", {"position": v(300, -1960) * mm});
            skPoint(sketch, "E34.0.79.0", {"position": v(350, -1985) * mm});
            skPoint(sketch, "E34.1.79.0", {"position": v(275, -1985) * mm});
            skPoint(sketch, "E34.2.79.0", {"position": v(325, -1985) * mm});
            skPoint(sketch, "E34.3.79.0", {"position": v(300, -1985) * mm});
            skSolve(sketch);
        }
        {
            var Q0;
            Q0=sQuery(id+"F16.wireOp",VERTEX,"E27.6.0.0");
            var Q1;
            Q1=sQuery(id+"F16.wireOp",VERTEX,"E30.1.0.1");
            var Q2;
            Q2=sQuery(id+"F16.wireOp",VERTEX,"E29.0.9.0");
            var Q3;
            Q3=sQuery(id+"F16.wireOp",VERTEX,"E30.2.0.1");
            var Q4;
            Q4=sQuery(id+"F16.wireOp",VERTEX,"E28.2.0.2");
            var Q5;
            Q5=sQuery(id+"F16.wireOp",VERTEX,"E27.1.0.0");
            var Q6;
            Q6=sQuery(id+"F16.wireOp",VERTEX,"E28.2.0.5");
            var Q7;
            Q7=sQuery(id+"F16.wireOp",VERTEX,"E29.0.8.0");
            var Q8;
            Q8=sQuery(id+"F16.wireOp",VERTEX,"E27.3.0.0");
            var Q9;
            Q9=sQuery(id+"F16.wireOp",VERTEX,"E30.1.0.3");
            var Q10;
            Q10=sQuery(id+"F16.wireOp",VERTEX,"E28.2.0.1");
            var Q11;
            Q11=sQuery(id+"F16.wireOp",VERTEX,"E28.1.0.0");
            var Q12;
            Q12=sQuery(id+"F16.wireOp",VERTEX,"E29.0.7.0");
            var Q13;
            Q13=sQuery(id+"F16.wireOp",VERTEX,"E30.1.0.2");
            var Q14;
            Q14=sQuery(id+"F16.wireOp",VERTEX,"E30.2.0.2");
            var Q15;
            Q15=sQuery(id+"F16.wireOp",VERTEX,"E28.2.0.3");
            var Q16;
            Q16=sQuery(id+"F16.wireOp",VERTEX,"E28.2.0.6");
            var Q17;
            Q17=sQuery(id+"F16.wireOp",VERTEX,"E28.1.0.2");
            var Q18;
            Q18=sQuery(id+"F16.wireOp",VERTEX,"E27.4.0.0");
            var Q19;
            Q19=sQuery(id+"F16.wireOp",VERTEX,"E28.1.0.6");
            var Q20;
            Q20=sQuery(id+"F16.wireOp",VERTEX,"E28.1.0.1");
            var Q21;
            Q21=sQuery(id+"F16.wireOp",VERTEX,"E30.2.0.3");
            var Q22;
            Q22=sQuery(id+"F16.wireOp",VERTEX,"E26");
            var Q23;
            Q23=sQuery(id+"F16.wireOp",VERTEX,"E28.1.0.5");
            var Q24;
            Q24=sQuery(id+"F16.wireOp",VERTEX,"E27.2.0.0");
            var Q25;
            Q25=sQuery(id+"F16.wireOp",VERTEX,"E27.5.0.0");
            var Q26;
            Q26=sQuery(id+"F16.wireOp",VERTEX,"E28.1.0.4");
            var Q27;
            Q27=sQuery(id+"F16.wireOp",VERTEX,"E28.1.0.3");
            var Q28;
            Q28=sQuery(id+"F16.wireOp",VERTEX,"E28.2.0.0");
            var Q29;
            Q29=sQuery(id+"F16.wireOp",VERTEX,"E28.2.0.4");
            var Q30;
            Q30=sQuery(id+"F16.wireOp",VERTEX,"E28.3.0.6");
            var Q31;
            Q31=sQuery(id+"F16.wireOp",VERTEX,"E28.3.0.4");
            var Q32;
            Q32=sQuery(id+"F16.wireOp",VERTEX,"E31.1.3.0");
            var Q33;
            Q33=sQuery(id+"F16.wireOp",VERTEX,"E31.3.3.0");
            var Q34;
            Q34=sQuery(id+"F16.wireOp",VERTEX,"E28.3.0.3");
            var Q35;
            Q35=sQuery(id+"F16.wireOp",VERTEX,"E28.3.0.5");
            var Q36;
            Q36=sQuery(id+"F16.wireOp",VERTEX,"E28.3.0.1");
            var Q37;
            Q37=sQuery(id+"F16.wireOp",VERTEX,"E31.2.3.0");
            var Q38;
            Q38=sQuery(id+"F16.wireOp",VERTEX,"E28.3.0.2");
            var Q39;
            Q39=sQuery(id+"F16.wireOp",VERTEX,"E28.4.0.2");
            var Q40;
            Q40=sQuery(id+"F16.wireOp",VERTEX,"E31.1.4.0");
            var Q41;
            Q41=sQuery(id+"F16.wireOp",VERTEX,"E31.1.5.0");
            var Q42;
            Q42=sQuery(id+"F16.wireOp",VERTEX,"E31.2.4.0");
            var Q43;
            Q43=sQuery(id+"F16.wireOp",VERTEX,"E28.4.0.5");
            var Q44;
            Q44=sQuery(id+"F16.wireOp",VERTEX,"E28.4.0.3");
            var Q45;
            Q45=sQuery(id+"F16.wireOp",VERTEX,"E28.5.0.4");
            var Q46;
            Q46=sQuery(id+"F16.wireOp",VERTEX,"E28.5.0.6");
            var Q47;
            Q47=sQuery(id+"F16.wireOp",VERTEX,"E28.5.0.5");
            var Q48;
            Q48=sQuery(id+"F16.wireOp",VERTEX,"E31.3.5.0");
            var Q49;
            Q49=sQuery(id+"F16.wireOp",VERTEX,"E28.4.0.4");
            var Q50;
            Q50=sQuery(id+"F16.wireOp",VERTEX,"E31.2.5.0");
            var Q51;
            Q51=sQuery(id+"F16.wireOp",VERTEX,"E28.5.0.3");
            var Q52;
            Q52=sQuery(id+"F16.wireOp",VERTEX,"E31.3.4.0");
            var Q53;
            Q53=sQuery(id+"F16.wireOp",VERTEX,"E28.4.0.6");
            var Q54;
            Q54=sQuery(id+"F16.wireOp",VERTEX,"E31.2.6.0");
            var Q55;
            Q55=sQuery(id+"F16.wireOp",VERTEX,"E28.6.0.6");
            var Q56;
            Q56=sQuery(id+"F16.wireOp",VERTEX,"E28.6.0.5");
            var Q57;
            Q57=sQuery(id+"F16.wireOp",VERTEX,"E31.3.6.0");
            var Q58;
            Q58=sQuery(id+"F16.wireOp",VERTEX,"E28.6.0.4");
            var Q59;
            Q59=sQuery(id+"F16.wireOp",VERTEX,"E31.1.6.0");
            var Q60;
            Q60=sQuery(id+"F16.wireOp",VERTEX,"E31.3.7.0");
            var Q61;
            Q61=sQuery(id+"F16.wireOp",VERTEX,"E31.2.7.0");
            var Q62;
            Q62=sQuery(id+"F16.wireOp",VERTEX,"E28.7.0.6");
            var Q63;
            Q63=sQuery(id+"F16.wireOp",VERTEX,"E28.7.0.5");
            var Q64;
            Q64=sQuery(id+"F16.wireOp",VERTEX,"E31.1.7.0");
            var Q65;
            Q65=sQuery(id+"F16.wireOp",VERTEX,"E31.2.10.0");
            var Q66;
            Q66=sQuery(id+"F16.wireOp",VERTEX,"E31.1.12.0");
            var Q67;
            Q67=sQuery(id+"F16.wireOp",VERTEX,"E31.1.10.0");
            var Q68;
            Q68=sQuery(id+"F16.wireOp",VERTEX,"E31.1.11.0");
            var Q69;
            Q69=sQuery(id+"F16.wireOp",VERTEX,"E28.8.0.6");
            var Q70;
            Q70=sQuery(id+"F16.wireOp",VERTEX,"E31.2.9.0");
            var Q71;
            Q71=sQuery(id+"F16.wireOp",VERTEX,"E31.1.8.0");
            var Q72;
            Q72=sQuery(id+"F16.wireOp",VERTEX,"E31.1.9.0");
            var Q73;
            Q73=sQuery(id+"F16.wireOp",VERTEX,"E31.2.8.0");
            var Q74;
            Q74=sQuery(id+"F16.wireOp",VERTEX,"E31.3.9.0");
            var Q75;
            Q75=sQuery(id+"F16.wireOp",VERTEX,"E31.3.8.0");
            var Q76;
            Q76=makeQuery(id+"F6.opExtrude","SWEPT_BODY",BODY,{"disambiguationData":[OSD([sQuery(id+"F0.wireOp",EDGE,"E23.5.0.1"),sQuery(id+"F0.wireOp",EDGE,"E23.5.0.2"),sQuery(id+"F0.wireOp",EDGE,"E23.5.0.3"),sQuery(id+"F0.wireOp",EDGE,"E23.5.0.4"),sQuery(id+"F0.wireOp",EDGE,"E23.5.0.11"),sQuery(id+"F0.wireOp",EDGE,"E23.5.0.12"),sQuery(id+"F0.wireOp",EDGE,"E23.5.0.13"),sQuery(id+"F0.wireOp",EDGE,"E23.5.0.14"),sQuery(id+"F0.wireOp",EDGE,"E23.5.0.15"),sQuery(id+"F0.wireOp",EDGE,"E23.5.0.16"),sQuery(id+"F0.wireOp",EDGE,"E23.5.0.18"),sQuery(id+"F0.wireOp",EDGE,"E23.5.0.19"),sQuery(id+"F0.wireOp",EDGE,"E23.5.0.20"),sQuery(id+"F0.wireOp",EDGE,"E23.5.0.21"),sQuery(id+"F0.wireOp",EDGE,"E23.5.0.22"),sQuery(id+"F0.wireOp",EDGE,"E23.5.0.23"),sQuery(id+"F0.wireOp",EDGE,"E23.5.0.24"),sQuery(id+"F0.wireOp",EDGE,"E23.5.0.25"),sQuery(id+"F0.wireOp",EDGE,"E23.5.0.26"),sQuery(id+"F0.wireOp",EDGE,"E23.5.0.27")])]});
            var Q77;
            Q77=makeQuery(id+"F10.opExtrude","SWEPT_BODY",BODY,{"disambiguationData":[OSD([sQuery(id+"F0.wireOp",EDGE,"E24.3.9.0"),sQuery(id+"F0.wireOp",EDGE,"E24.6.9.0"),sQuery(id+"F0.wireOp",EDGE,"E24.9.9.0"),sQuery(id+"F0.wireOp",EDGE,"E24.12.9.0"),sQuery(id+"F0.wireOp",EDGE,"E24.21.9.0"),sQuery(id+"F0.wireOp",EDGE,"E24.24.9.0"),sQuery(id+"F0.wireOp",EDGE,"E24.27.9.0"),sQuery(id+"F0.wireOp",EDGE,"E24.30.9.0"),sQuery(id+"F0.wireOp",EDGE,"E24.33.9.0"),sQuery(id+"F0.wireOp",EDGE,"E24.36.9.0"),sQuery(id+"F0.wireOp",EDGE,"E24.43.9.0"),sQuery(id+"F0.wireOp",EDGE,"E24.46.9.0"),sQuery(id+"F0.wireOp",EDGE,"E24.49.9.0"),sQuery(id+"F0.wireOp",EDGE,"E24.52.9.0"),sQuery(id+"F0.wireOp",EDGE,"E24.56.9.0"),sQuery(id+"F0.wireOp",EDGE,"E24.59.9.0"),sQuery(id+"F0.wireOp",EDGE,"E24.63.9.0"),sQuery(id+"F0.wireOp",EDGE,"E24.66.9.0"),sQuery(id+"F0.wireOp",EDGE,"E24.70.9.0"),sQuery(id+"F0.wireOp",EDGE,"E24.74.9.0")])]});
            var Q78;
            Q78=makeQuery(id+"F2.opExtrude","SWEPT_BODY",BODY,{"disambiguationData":[OSD([sQuery(id+"F0.wireOp",EDGE,"E23.1.0.1"),sQuery(id+"F0.wireOp",EDGE,"E23.1.0.2"),sQuery(id+"F0.wireOp",EDGE,"E23.1.0.3"),sQuery(id+"F0.wireOp",EDGE,"E23.1.0.4"),sQuery(id+"F0.wireOp",EDGE,"E23.1.0.11"),sQuery(id+"F0.wireOp",EDGE,"E23.1.0.12"),sQuery(id+"F0.wireOp",EDGE,"E23.1.0.13"),sQuery(id+"F0.wireOp",EDGE,"E23.1.0.14"),sQuery(id+"F0.wireOp",EDGE,"E23.1.0.15"),sQuery(id+"F0.wireOp",EDGE,"E23.1.0.16"),sQuery(id+"F0.wireOp",EDGE,"E23.1.0.18"),sQuery(id+"F0.wireOp",EDGE,"E23.1.0.19"),sQuery(id+"F0.wireOp",EDGE,"E23.1.0.20"),sQuery(id+"F0.wireOp",EDGE,"E23.1.0.21"),sQuery(id+"F0.wireOp",EDGE,"E23.1.0.22"),sQuery(id+"F0.wireOp",EDGE,"E23.1.0.23"),sQuery(id+"F0.wireOp",EDGE,"E23.1.0.24"),sQuery(id+"F0.wireOp",EDGE,"E23.1.0.25"),sQuery(id+"F0.wireOp",EDGE,"E23.1.0.26"),sQuery(id+"F0.wireOp",EDGE,"E23.1.0.27")])]});
            var Q79;
            Q79=makeQuery(id+"F5.opExtrude","SWEPT_BODY",BODY,{"disambiguationData":[OSD([sQuery(id+"F0.wireOp",EDGE,"E23.4.0.1"),sQuery(id+"F0.wireOp",EDGE,"E23.4.0.2"),sQuery(id+"F0.wireOp",EDGE,"E23.4.0.3"),sQuery(id+"F0.wireOp",EDGE,"E23.4.0.4"),sQuery(id+"F0.wireOp",EDGE,"E23.4.0.11"),sQuery(id+"F0.wireOp",EDGE,"E23.4.0.12"),sQuery(id+"F0.wireOp",EDGE,"E23.4.0.13"),sQuery(id+"F0.wireOp",EDGE,"E23.4.0.14"),sQuery(id+"F0.wireOp",EDGE,"E23.4.0.15"),sQuery(id+"F0.wireOp",EDGE,"E23.4.0.16"),sQuery(id+"F0.wireOp",EDGE,"E23.4.0.18"),sQuery(id+"F0.wireOp",EDGE,"E23.4.0.19"),sQuery(id+"F0.wireOp",EDGE,"E23.4.0.20"),sQuery(id+"F0.wireOp",EDGE,"E23.4.0.21"),sQuery(id+"F0.wireOp",EDGE,"E23.4.0.22"),sQuery(id+"F0.wireOp",EDGE,"E23.4.0.23"),sQuery(id+"F0.wireOp",EDGE,"E23.4.0.24"),sQuery(id+"F0.wireOp",EDGE,"E23.4.0.25"),sQuery(id+"F0.wireOp",EDGE,"E23.4.0.26"),sQuery(id+"F0.wireOp",EDGE,"E23.4.0.27")])]});
            var Q80;
            Q80=makeQuery(id+"F11.opExtrude","SWEPT_BODY",BODY,{"disambiguationData":[OSD([sQuery(id+"F0.wireOp",EDGE,"E24.3.10.0"),sQuery(id+"F0.wireOp",EDGE,"E24.6.10.0"),sQuery(id+"F0.wireOp",EDGE,"E24.9.10.0"),sQuery(id+"F0.wireOp",EDGE,"E24.12.10.0"),sQuery(id+"F0.wireOp",EDGE,"E24.21.10.0"),sQuery(id+"F0.wireOp",EDGE,"E24.24.10.0"),sQuery(id+"F0.wireOp",EDGE,"E24.27.10.0"),sQuery(id+"F0.wireOp",EDGE,"E24.30.10.0"),sQuery(id+"F0.wireOp",EDGE,"E24.33.10.0"),sQuery(id+"F0.wireOp",EDGE,"E24.36.10.0"),sQuery(id+"F0.wireOp",EDGE,"E24.43.10.0"),sQuery(id+"F0.wireOp",EDGE,"E24.46.10.0"),sQuery(id+"F0.wireOp",EDGE,"E24.49.10.0"),sQuery(id+"F0.wireOp",EDGE,"E24.52.10.0"),sQuery(id+"F0.wireOp",EDGE,"E24.56.10.0"),sQuery(id+"F0.wireOp",EDGE,"E24.59.10.0"),sQuery(id+"F0.wireOp",EDGE,"E24.63.10.0"),sQuery(id+"F0.wireOp",EDGE,"E24.66.10.0"),sQuery(id+"F0.wireOp",EDGE,"E24.70.10.0"),sQuery(id+"F0.wireOp",EDGE,"E24.74.10.0")])]});
            var Q81;
            Q81=makeQuery(id+"F7.opExtrude","SWEPT_BODY",BODY,{"disambiguationData":[OSD([sQuery(id+"F0.wireOp",EDGE,"E23.6.0.1"),sQuery(id+"F0.wireOp",EDGE,"E23.6.0.2"),sQuery(id+"F0.wireOp",EDGE,"E23.6.0.3"),sQuery(id+"F0.wireOp",EDGE,"E23.6.0.4"),sQuery(id+"F0.wireOp",EDGE,"E23.6.0.11"),sQuery(id+"F0.wireOp",EDGE,"E23.6.0.12"),sQuery(id+"F0.wireOp",EDGE,"E23.6.0.13"),sQuery(id+"F0.wireOp",EDGE,"E23.6.0.14"),sQuery(id+"F0.wireOp",EDGE,"E23.6.0.15"),sQuery(id+"F0.wireOp",EDGE,"E23.6.0.16"),sQuery(id+"F0.wireOp",EDGE,"E23.6.0.18"),sQuery(id+"F0.wireOp",EDGE,"E23.6.0.19"),sQuery(id+"F0.wireOp",EDGE,"E23.6.0.20"),sQuery(id+"F0.wireOp",EDGE,"E23.6.0.21"),sQuery(id+"F0.wireOp",EDGE,"E23.6.0.22"),sQuery(id+"F0.wireOp",EDGE,"E23.6.0.23"),sQuery(id+"F0.wireOp",EDGE,"E23.6.0.24"),sQuery(id+"F0.wireOp",EDGE,"E23.6.0.25"),sQuery(id+"F0.wireOp",EDGE,"E23.6.0.26"),sQuery(id+"F0.wireOp",EDGE,"E23.6.0.27")])]});
            var Q82;
            Q82=makeQuery(id+"F9.opExtrude","SWEPT_BODY",BODY,{"disambiguationData":[OSD([sQuery(id+"F0.wireOp",EDGE,"E24.3.8.0"),sQuery(id+"F0.wireOp",EDGE,"E24.6.8.0"),sQuery(id+"F0.wireOp",EDGE,"E24.9.8.0"),sQuery(id+"F0.wireOp",EDGE,"E24.12.8.0"),sQuery(id+"F0.wireOp",EDGE,"E24.21.8.0"),sQuery(id+"F0.wireOp",EDGE,"E24.24.8.0"),sQuery(id+"F0.wireOp",EDGE,"E24.27.8.0"),sQuery(id+"F0.wireOp",EDGE,"E24.30.8.0"),sQuery(id+"F0.wireOp",EDGE,"E24.33.8.0"),sQuery(id+"F0.wireOp",EDGE,"E24.36.8.0"),sQuery(id+"F0.wireOp",EDGE,"E24.43.8.0"),sQuery(id+"F0.wireOp",EDGE,"E24.46.8.0"),sQuery(id+"F0.wireOp",EDGE,"E24.49.8.0"),sQuery(id+"F0.wireOp",EDGE,"E24.52.8.0"),sQuery(id+"F0.wireOp",EDGE,"E24.56.8.0"),sQuery(id+"F0.wireOp",EDGE,"E24.59.8.0"),sQuery(id+"F0.wireOp",EDGE,"E24.63.8.0"),sQuery(id+"F0.wireOp",EDGE,"E24.66.8.0"),sQuery(id+"F0.wireOp",EDGE,"E24.70.8.0"),sQuery(id+"F0.wireOp",EDGE,"E24.74.8.0")])]});
            var Q83;
            Q83=makeQuery(id+"F3.opExtrude","SWEPT_BODY",BODY,{"disambiguationData":[OSD([sQuery(id+"F0.wireOp",EDGE,"E23.2.0.1"),sQuery(id+"F0.wireOp",EDGE,"E23.2.0.2"),sQuery(id+"F0.wireOp",EDGE,"E23.2.0.3"),sQuery(id+"F0.wireOp",EDGE,"E23.2.0.4"),sQuery(id+"F0.wireOp",EDGE,"E23.2.0.11"),sQuery(id+"F0.wireOp",EDGE,"E23.2.0.12"),sQuery(id+"F0.wireOp",EDGE,"E23.2.0.13"),sQuery(id+"F0.wireOp",EDGE,"E23.2.0.14"),sQuery(id+"F0.wireOp",EDGE,"E23.2.0.15"),sQuery(id+"F0.wireOp",EDGE,"E23.2.0.16"),sQuery(id+"F0.wireOp",EDGE,"E23.2.0.18"),sQuery(id+"F0.wireOp",EDGE,"E23.2.0.19"),sQuery(id+"F0.wireOp",EDGE,"E23.2.0.20"),sQuery(id+"F0.wireOp",EDGE,"E23.2.0.21"),sQuery(id+"F0.wireOp",EDGE,"E23.2.0.22"),sQuery(id+"F0.wireOp",EDGE,"E23.2.0.23"),sQuery(id+"F0.wireOp",EDGE,"E23.2.0.24"),sQuery(id+"F0.wireOp",EDGE,"E23.2.0.25"),sQuery(id+"F0.wireOp",EDGE,"E23.2.0.26"),sQuery(id+"F0.wireOp",EDGE,"E23.2.0.27")])]});
            var Q84;
            Q84=makeQuery(id+"F8.opExtrude","SWEPT_BODY",BODY,{"disambiguationData":[OSD([sQuery(id+"F0.wireOp",EDGE,"E24.3.7.0"),sQuery(id+"F0.wireOp",EDGE,"E24.6.7.0"),sQuery(id+"F0.wireOp",EDGE,"E24.9.7.0"),sQuery(id+"F0.wireOp",EDGE,"E24.12.7.0"),sQuery(id+"F0.wireOp",EDGE,"E24.21.7.0"),sQuery(id+"F0.wireOp",EDGE,"E24.24.7.0"),sQuery(id+"F0.wireOp",EDGE,"E24.27.7.0"),sQuery(id+"F0.wireOp",EDGE,"E24.30.7.0"),sQuery(id+"F0.wireOp",EDGE,"E24.33.7.0"),sQuery(id+"F0.wireOp",EDGE,"E24.36.7.0"),sQuery(id+"F0.wireOp",EDGE,"E24.43.7.0"),sQuery(id+"F0.wireOp",EDGE,"E24.46.7.0"),sQuery(id+"F0.wireOp",EDGE,"E24.49.7.0"),sQuery(id+"F0.wireOp",EDGE,"E24.52.7.0"),sQuery(id+"F0.wireOp",EDGE,"E24.56.7.0"),sQuery(id+"F0.wireOp",EDGE,"E24.59.7.0"),sQuery(id+"F0.wireOp",EDGE,"E24.63.7.0"),sQuery(id+"F0.wireOp",EDGE,"E24.66.7.0"),sQuery(id+"F0.wireOp",EDGE,"E24.70.7.0"),sQuery(id+"F0.wireOp",EDGE,"E24.74.7.0")])]});
            var Q85;
            Q85=makeQuery(id+"F1.opExtrude","SWEPT_BODY",BODY,{"disambiguationData":[OSD([sQuery(id+"F0.wireOp",EDGE,"E1.bottom"),sQuery(id+"F0.wireOp",EDGE,"E1.top"),sQuery(id+"F0.wireOp",EDGE,"E1.left"),sQuery(id+"F0.wireOp",EDGE,"E1.right"),sQuery(id+"F0.wireOp",EDGE,"E2"),sQuery(id+"F0.wireOp",EDGE,"E3"),sQuery(id+"F0.wireOp",EDGE,"E4"),sQuery(id+"F0.wireOp",EDGE,"E5"),sQuery(id+"F0.wireOp",EDGE,"E6"),sQuery(id+"F0.wireOp",EDGE,"E7"),sQuery(id+"F0.wireOp",EDGE,"E8"),sQuery(id+"F0.wireOp",EDGE,"E9.MirrorCS"),sQuery(id+"F0.wireOp",EDGE,"E10.MirrorCS"),sQuery(id+"F0.wireOp",EDGE,"E11.MirrorCS"),sQuery(id+"F0.wireOp",EDGE,"E13.trimOffspring"),sQuery(id+"F0.wireOp",EDGE,"E14.trimOffspring"),sQuery(id+"F0.wireOp",EDGE,"E16.trimOffspring"),sQuery(id+"F0.wireOp",EDGE,"E17.trimOffspring"),sQuery(id+"F0.wireOp",EDGE,"E20"),sQuery(id+"F0.wireOp",EDGE,"E21")])]});
            var Q86;
            Q86=makeQuery(id+"F4.opExtrude","SWEPT_BODY",BODY,{"disambiguationData":[OSD([sQuery(id+"F0.wireOp",EDGE,"E23.3.0.1"),sQuery(id+"F0.wireOp",EDGE,"E23.3.0.2"),sQuery(id+"F0.wireOp",EDGE,"E23.3.0.3"),sQuery(id+"F0.wireOp",EDGE,"E23.3.0.4"),sQuery(id+"F0.wireOp",EDGE,"E23.3.0.11"),sQuery(id+"F0.wireOp",EDGE,"E23.3.0.12"),sQuery(id+"F0.wireOp",EDGE,"E23.3.0.13"),sQuery(id+"F0.wireOp",EDGE,"E23.3.0.14"),sQuery(id+"F0.wireOp",EDGE,"E23.3.0.15"),sQuery(id+"F0.wireOp",EDGE,"E23.3.0.16"),sQuery(id+"F0.wireOp",EDGE,"E23.3.0.18"),sQuery(id+"F0.wireOp",EDGE,"E23.3.0.19"),sQuery(id+"F0.wireOp",EDGE,"E23.3.0.20"),sQuery(id+"F0.wireOp",EDGE,"E23.3.0.21"),sQuery(id+"F0.wireOp",EDGE,"E23.3.0.22"),sQuery(id+"F0.wireOp",EDGE,"E23.3.0.23"),sQuery(id+"F0.wireOp",EDGE,"E23.3.0.24"),sQuery(id+"F0.wireOp",EDGE,"E23.3.0.25"),sQuery(id+"F0.wireOp",EDGE,"E23.3.0.26"),sQuery(id+"F0.wireOp",EDGE,"E23.3.0.27")])]});
            hole(context, id + "F17", {"style" : HoleStyle.C_BORE, "endStyle" : HoleEndStyle.THROUGH, "holeDiameter" : 3.5 * mm, "cBoreDiameter" : 6 * mm, "cBoreDepth" : 4.5 * mm, "majorDiameter" : 5 * mm, "isTappedThrough" : true, "tappedDepth" : 12 * mm, "tapClearance" : 3, "locations" : qUnion([Q0, Q1, Q2, Q3, Q4, Q5, Q6, Q7, Q8, Q9, Q10, Q11, Q12, Q13, Q14, Q15, Q16, Q17, Q18, Q19, Q20, Q21, Q22, Q23, Q24, Q25, Q26, Q27, Q28, Q29, Q30, Q31, Q32, Q33, Q34, Q35, Q36, Q37, Q38, Q39, Q40, Q41, Q42, Q43, Q44, Q45, Q46, Q47, Q48, Q49, Q50, Q51, Q52, Q53, Q54, Q55, Q56, Q57, Q58, Q59, Q60, Q61, Q62, Q63, Q64, Q65, Q66, Q67, Q68, Q69, Q70, Q71, Q72, Q73, Q74, Q75]), "scope" : qUnion([Q76, Q77, Q78, Q79, Q80, Q81, Q82, Q83, Q84, Q85, Q86])});
        }
        {
            var Q0;
            Q0=sQuery(id+"F16.wireOp",VERTEX,"E31.0.3.0");
            var Q1;
            Q1=sQuery(id+"F16.wireOp",VERTEX,"E31.0.4.0");
            var Q2;
            Q2=sQuery(id+"F16.wireOp",VERTEX,"E31.0.8.0");
            var Q3;
            Q3=sQuery(id+"F16.wireOp",VERTEX,"E31.0.7.0");
            var Q4;
            Q4=sQuery(id+"F16.wireOp",VERTEX,"E31.0.10.0");
            var Q5;
            Q5=sQuery(id+"F16.wireOp",VERTEX,"E31.0.12.0");
            var Q6;
            Q6=sQuery(id+"F16.wireOp",VERTEX,"E31.0.5.0");
            var Q7;
            Q7=sQuery(id+"F16.wireOp",VERTEX,"E30.1.0.0");
            var Q8;
            Q8=sQuery(id+"F16.wireOp",VERTEX,"E31.0.11.0");
            var Q9;
            Q9=sQuery(id+"F16.wireOp",VERTEX,"E31.0.14.0");
            var Q10;
            Q10=sQuery(id+"F16.wireOp",VERTEX,"E30.2.0.0");
            var Q11;
            Q11=sQuery(id+"F16.wireOp",VERTEX,"E31.0.6.0");
            var Q12;
            Q12=sQuery(id+"F16.wireOp",VERTEX,"E29.0.10.0");
            var Q13;
            Q13=sQuery(id+"F16.wireOp",VERTEX,"E31.0.9.0");
            var Q14;
            Q14=sQuery(id+"F16.wireOp",VERTEX,"E31.0.13.0");
            var Q15;
            Q15=sQuery(id+"F16.wireOp",VERTEX,"E34.1.18.0");
            var Q16;
            Q16=sQuery(id+"F16.wireOp",VERTEX,"E33.2.0.1");
            var Q17;
            Q17=sQuery(id+"F16.wireOp",VERTEX,"E34.1.11.0");
            var Q18;
            Q18=sQuery(id+"F16.wireOp",VERTEX,"E32.0.11.0");
            var Q19;
            Q19=sQuery(id+"F16.wireOp",VERTEX,"E34.1.16.0");
            var Q20;
            Q20=sQuery(id+"F16.wireOp",VERTEX,"E34.1.8.0");
            var Q21;
            Q21=sQuery(id+"F16.wireOp",VERTEX,"E33.1.0.1");
            var Q22;
            Q22=sQuery(id+"F16.wireOp",VERTEX,"E34.1.17.0");
            var Q23;
            Q23=sQuery(id+"F16.wireOp",VERTEX,"E34.1.13.0");
            var Q24;
            Q24=sQuery(id+"F16.wireOp",VERTEX,"E34.1.9.0");
            var Q25;
            Q25=sQuery(id+"F16.wireOp",VERTEX,"E34.1.5.0");
            var Q26;
            Q26=sQuery(id+"F16.wireOp",VERTEX,"E34.1.12.0");
            var Q27;
            Q27=sQuery(id+"F16.wireOp",VERTEX,"E34.1.4.0");
            var Q28;
            Q28=sQuery(id+"F16.wireOp",VERTEX,"E34.1.15.0");
            var Q29;
            Q29=sQuery(id+"F16.wireOp",VERTEX,"E34.1.7.0");
            var Q30;
            Q30=sQuery(id+"F16.wireOp",VERTEX,"E34.1.6.0");
            var Q31;
            Q31=sQuery(id+"F16.wireOp",VERTEX,"E34.1.3.0");
            var Q32;
            Q32=sQuery(id+"F16.wireOp",VERTEX,"E34.1.14.0");
            var Q33;
            Q33=sQuery(id+"F16.wireOp",VERTEX,"E34.1.10.0");
            var Q34;
            Q34=sQuery(id+"F16.wireOp",VERTEX,"E34.3.16.0");
            var Q35;
            Q35=sQuery(id+"F16.wireOp",VERTEX,"E34.3.12.0");
            var Q36;
            Q36=sQuery(id+"F16.wireOp",VERTEX,"E34.3.21.0");
            var Q37;
            Q37=sQuery(id+"F16.wireOp",VERTEX,"E34.3.20.0");
            var Q38;
            Q38=sQuery(id+"F16.wireOp",VERTEX,"E34.3.9.0");
            var Q39;
            Q39=sQuery(id+"F16.wireOp",VERTEX,"E34.3.13.0");
            var Q40;
            Q40=sQuery(id+"F16.wireOp",VERTEX,"E34.3.10.0");
            var Q41;
            Q41=sQuery(id+"F16.wireOp",VERTEX,"E34.3.15.0");
            var Q42;
            Q42=sQuery(id+"F16.wireOp",VERTEX,"E34.3.4.0");
            var Q43;
            Q43=sQuery(id+"F16.wireOp",VERTEX,"E33.1.0.3");
            var Q44;
            Q44=sQuery(id+"F16.wireOp",VERTEX,"E34.3.8.0");
            var Q45;
            Q45=sQuery(id+"F16.wireOp",VERTEX,"E34.3.19.0");
            var Q46;
            Q46=sQuery(id+"F16.wireOp",VERTEX,"E34.3.3.0");
            var Q47;
            Q47=sQuery(id+"F16.wireOp",VERTEX,"E34.3.7.0");
            var Q48;
            Q48=sQuery(id+"F16.wireOp",VERTEX,"E34.3.18.0");
            var Q49;
            Q49=sQuery(id+"F16.wireOp",VERTEX,"E34.3.22.0");
            var Q50;
            Q50=sQuery(id+"F16.wireOp",VERTEX,"E33.2.0.3");
            var Q51;
            Q51=sQuery(id+"F16.wireOp",VERTEX,"E34.3.6.0");
            var Q52;
            Q52=sQuery(id+"F16.wireOp",VERTEX,"E34.3.17.0");
            var Q53;
            Q53=sQuery(id+"F16.wireOp",VERTEX,"E34.3.14.0");
            var Q54;
            Q54=sQuery(id+"F16.wireOp",VERTEX,"E32.0.12.0");
            var Q55;
            Q55=sQuery(id+"F16.wireOp",VERTEX,"E34.3.5.0");
            var Q56;
            Q56=sQuery(id+"F16.wireOp",VERTEX,"E34.3.11.0");
            var Q57;
            Q57=sQuery(id+"F16.wireOp",VERTEX,"E33.2.0.2");
            var Q58;
            Q58=sQuery(id+"F16.wireOp",VERTEX,"E34.2.25.0");
            var Q59;
            Q59=sQuery(id+"F16.wireOp",VERTEX,"E34.2.16.0");
            var Q60;
            Q60=sQuery(id+"F16.wireOp",VERTEX,"E34.2.21.0");
            var Q61;
            Q61=sQuery(id+"F16.wireOp",VERTEX,"E34.2.13.0");
            var Q62;
            Q62=sQuery(id+"F16.wireOp",VERTEX,"E34.2.10.0");
            var Q63;
            Q63=sQuery(id+"F16.wireOp",VERTEX,"E34.2.22.0");
            var Q64;
            Q64=sQuery(id+"F16.wireOp",VERTEX,"E34.2.15.0");
            var Q65;
            Q65=sQuery(id+"F16.wireOp",VERTEX,"E34.2.26.0");
            var Q66;
            Q66=sQuery(id+"F16.wireOp",VERTEX,"E34.2.4.0");
            var Q67;
            Q67=sQuery(id+"F16.wireOp",VERTEX,"E32.0.13.0");
            var Q68;
            Q68=sQuery(id+"F16.wireOp",VERTEX,"E34.2.17.0");
            var Q69;
            Q69=sQuery(id+"F16.wireOp",VERTEX,"E34.2.5.0");
            var Q70;
            Q70=sQuery(id+"F16.wireOp",VERTEX,"E34.2.6.0");
            var Q71;
            Q71=sQuery(id+"F16.wireOp",VERTEX,"E33.1.0.2");
            var Q72;
            Q72=sQuery(id+"F16.wireOp",VERTEX,"E34.2.7.0");
            var Q73;
            Q73=sQuery(id+"F16.wireOp",VERTEX,"E34.2.18.0");
            var Q74;
            Q74=sQuery(id+"F16.wireOp",VERTEX,"E34.2.20.0");
            var Q75;
            Q75=sQuery(id+"F16.wireOp",VERTEX,"E34.2.12.0");
            var Q76;
            Q76=sQuery(id+"F16.wireOp",VERTEX,"E34.2.11.0");
            var Q77;
            Q77=sQuery(id+"F16.wireOp",VERTEX,"E34.2.9.0");
            var Q78;
            Q78=sQuery(id+"F16.wireOp",VERTEX,"E34.2.23.0");
            var Q79;
            Q79=sQuery(id+"F16.wireOp",VERTEX,"E34.2.24.0");
            var Q80;
            Q80=sQuery(id+"F16.wireOp",VERTEX,"E34.2.14.0");
            var Q81;
            Q81=sQuery(id+"F16.wireOp",VERTEX,"E34.2.27.0");
            var Q82;
            Q82=sQuery(id+"F16.wireOp",VERTEX,"E34.2.3.0");
            var Q83;
            Q83=sQuery(id+"F16.wireOp",VERTEX,"E34.2.19.0");
            var Q84;
            Q84=sQuery(id+"F16.wireOp",VERTEX,"E34.2.8.0");
            var Q85;
            Q85=makeQuery(id+"F11.opExtrude","SWEPT_BODY",BODY,{"disambiguationData":[OSD([sQuery(id+"F0.wireOp",EDGE,"E24.3.10.0"),sQuery(id+"F0.wireOp",EDGE,"E24.6.10.0"),sQuery(id+"F0.wireOp",EDGE,"E24.9.10.0"),sQuery(id+"F0.wireOp",EDGE,"E24.12.10.0"),sQuery(id+"F0.wireOp",EDGE,"E24.21.10.0"),sQuery(id+"F0.wireOp",EDGE,"E24.24.10.0"),sQuery(id+"F0.wireOp",EDGE,"E24.27.10.0"),sQuery(id+"F0.wireOp",EDGE,"E24.30.10.0"),sQuery(id+"F0.wireOp",EDGE,"E24.33.10.0"),sQuery(id+"F0.wireOp",EDGE,"E24.36.10.0"),sQuery(id+"F0.wireOp",EDGE,"E24.43.10.0"),sQuery(id+"F0.wireOp",EDGE,"E24.46.10.0"),sQuery(id+"F0.wireOp",EDGE,"E24.49.10.0"),sQuery(id+"F0.wireOp",EDGE,"E24.52.10.0"),sQuery(id+"F0.wireOp",EDGE,"E24.56.10.0"),sQuery(id+"F0.wireOp",EDGE,"E24.59.10.0"),sQuery(id+"F0.wireOp",EDGE,"E24.63.10.0"),sQuery(id+"F0.wireOp",EDGE,"E24.66.10.0"),sQuery(id+"F0.wireOp",EDGE,"E24.70.10.0"),sQuery(id+"F0.wireOp",EDGE,"E24.74.10.0")])]});
            var Q86;
            Q86=makeQuery(id+"F12.opExtrude","SWEPT_BODY",BODY,{"disambiguationData":[OSD([sQuery(id+"F0.wireOp",EDGE,"E25.3.11.0"),sQuery(id+"F0.wireOp",EDGE,"E25.6.11.0"),sQuery(id+"F0.wireOp",EDGE,"E25.9.11.0"),sQuery(id+"F0.wireOp",EDGE,"E25.12.11.0"),sQuery(id+"F0.wireOp",EDGE,"E25.21.11.0"),sQuery(id+"F0.wireOp",EDGE,"E25.24.11.0"),sQuery(id+"F0.wireOp",EDGE,"E25.27.11.0"),sQuery(id+"F0.wireOp",EDGE,"E25.30.11.0"),sQuery(id+"F0.wireOp",EDGE,"E25.33.11.0"),sQuery(id+"F0.wireOp",EDGE,"E25.36.11.0"),sQuery(id+"F0.wireOp",EDGE,"E25.43.11.0"),sQuery(id+"F0.wireOp",EDGE,"E25.46.11.0"),sQuery(id+"F0.wireOp",EDGE,"E25.49.11.0"),sQuery(id+"F0.wireOp",EDGE,"E25.52.11.0"),sQuery(id+"F0.wireOp",EDGE,"E25.56.11.0"),sQuery(id+"F0.wireOp",EDGE,"E25.59.11.0"),sQuery(id+"F0.wireOp",EDGE,"E25.63.11.0"),sQuery(id+"F0.wireOp",EDGE,"E25.66.11.0"),sQuery(id+"F0.wireOp",EDGE,"E25.70.11.0"),sQuery(id+"F0.wireOp",EDGE,"E25.74.11.0")])]});
            var Q87;
            Q87=makeQuery(id+"F13.opExtrude","SWEPT_BODY",BODY,{"disambiguationData":[OSD([sQuery(id+"F0.wireOp",EDGE,"E25.3.12.0"),sQuery(id+"F0.wireOp",EDGE,"E25.6.12.0"),sQuery(id+"F0.wireOp",EDGE,"E25.9.12.0"),sQuery(id+"F0.wireOp",EDGE,"E25.12.12.0"),sQuery(id+"F0.wireOp",EDGE,"E25.21.12.0"),sQuery(id+"F0.wireOp",EDGE,"E25.24.12.0"),sQuery(id+"F0.wireOp",EDGE,"E25.27.12.0"),sQuery(id+"F0.wireOp",EDGE,"E25.30.12.0"),sQuery(id+"F0.wireOp",EDGE,"E25.33.12.0"),sQuery(id+"F0.wireOp",EDGE,"E25.36.12.0"),sQuery(id+"F0.wireOp",EDGE,"E25.43.12.0"),sQuery(id+"F0.wireOp",EDGE,"E25.46.12.0"),sQuery(id+"F0.wireOp",EDGE,"E25.49.12.0"),sQuery(id+"F0.wireOp",EDGE,"E25.52.12.0"),sQuery(id+"F0.wireOp",EDGE,"E25.56.12.0"),sQuery(id+"F0.wireOp",EDGE,"E25.59.12.0"),sQuery(id+"F0.wireOp",EDGE,"E25.63.12.0"),sQuery(id+"F0.wireOp",EDGE,"E25.66.12.0"),sQuery(id+"F0.wireOp",EDGE,"E25.70.12.0"),sQuery(id+"F0.wireOp",EDGE,"E25.74.12.0")])]});
            var Q88;
            Q88=makeQuery(id+"F14.opExtrude","SWEPT_BODY",BODY,{"disambiguationData":[OSD([sQuery(id+"F0.wireOp",EDGE,"E25.3.13.0"),sQuery(id+"F0.wireOp",EDGE,"E25.6.13.0"),sQuery(id+"F0.wireOp",EDGE,"E25.9.13.0"),sQuery(id+"F0.wireOp",EDGE,"E25.12.13.0"),sQuery(id+"F0.wireOp",EDGE,"E25.21.13.0"),sQuery(id+"F0.wireOp",EDGE,"E25.24.13.0"),sQuery(id+"F0.wireOp",EDGE,"E25.27.13.0"),sQuery(id+"F0.wireOp",EDGE,"E25.30.13.0"),sQuery(id+"F0.wireOp",EDGE,"E25.33.13.0"),sQuery(id+"F0.wireOp",EDGE,"E25.36.13.0"),sQuery(id+"F0.wireOp",EDGE,"E25.43.13.0"),sQuery(id+"F0.wireOp",EDGE,"E25.46.13.0"),sQuery(id+"F0.wireOp",EDGE,"E25.49.13.0"),sQuery(id+"F0.wireOp",EDGE,"E25.52.13.0"),sQuery(id+"F0.wireOp",EDGE,"E25.56.13.0"),sQuery(id+"F0.wireOp",EDGE,"E25.59.13.0"),sQuery(id+"F0.wireOp",EDGE,"E25.63.13.0"),sQuery(id+"F0.wireOp",EDGE,"E25.66.13.0"),sQuery(id+"F0.wireOp",EDGE,"E25.70.13.0"),sQuery(id+"F0.wireOp",EDGE,"E25.74.13.0")])]});
            hole(context, id + "F18", {"style" : HoleStyle.C_BORE, "endStyle" : HoleEndStyle.THROUGH, "holeDiameter" : 3.5 * mm, "cBoreDiameter" : 6 * mm, "cBoreDepth" : 4.5 * mm, "majorDiameter" : 5 * mm, "isTappedThrough" : true, "tappedDepth" : 12 * mm, "tapClearance" : 3, "locations" : qUnion([Q0, Q1, Q2, Q3, Q4, Q5, Q6, Q7, Q8, Q9, Q10, Q11, Q12, Q13, Q14, Q15, Q16, Q17, Q18, Q19, Q20, Q21, Q22, Q23, Q24, Q25, Q26, Q27, Q28, Q29, Q30, Q31, Q32, Q33, Q34, Q35, Q36, Q37, Q38, Q39, Q40, Q41, Q42, Q43, Q44, Q45, Q46, Q47, Q48, Q49, Q50, Q51, Q52, Q53, Q54, Q55, Q56, Q57, Q58, Q59, Q60, Q61, Q62, Q63, Q64, Q65, Q66, Q67, Q68, Q69, Q70, Q71, Q72, Q73, Q74, Q75, Q76, Q77, Q78, Q79, Q80, Q81, Q82, Q83, Q84]), "scope" : qUnion([Q85, Q86, Q87, Q88])});
        }
        {
            var Q0;
            Q0=sQuery(id+"F16.wireOp",VERTEX,"E34.0.12.0");
            var Q1;
            Q1=sQuery(id+"F16.wireOp",VERTEX,"E34.0.6.0");
            var Q2;
            Q2=sQuery(id+"F16.wireOp",VERTEX,"E34.0.4.0");
            var Q3;
            Q3=sQuery(id+"F16.wireOp",VERTEX,"E34.0.10.0");
            var Q4;
            Q4=sQuery(id+"F16.wireOp",VERTEX,"E34.0.13.0");
            var Q5;
            Q5=sQuery(id+"F16.wireOp",VERTEX,"E34.0.8.0");
            var Q6;
            Q6=sQuery(id+"F16.wireOp",VERTEX,"E34.0.18.0");
            var Q7;
            Q7=sQuery(id+"F16.wireOp",VERTEX,"E32.0.14.0");
            var Q8;
            Q8=sQuery(id+"F16.wireOp",VERTEX,"E34.0.25.0");
            var Q9;
            Q9=sQuery(id+"F16.wireOp",VERTEX,"E34.0.22.0");
            var Q10;
            Q10=sQuery(id+"F16.wireOp",VERTEX,"E34.0.9.0");
            var Q11;
            Q11=sQuery(id+"F16.wireOp",VERTEX,"E34.0.24.0");
            var Q12;
            Q12=sQuery(id+"F16.wireOp",VERTEX,"E34.0.17.0");
            var Q13;
            Q13=sQuery(id+"F16.wireOp",VERTEX,"E34.0.16.0");
            var Q14;
            Q14=sQuery(id+"F16.wireOp",VERTEX,"E34.0.29.0");
            var Q15;
            Q15=sQuery(id+"F16.wireOp",VERTEX,"E34.0.26.0");
            var Q16;
            Q16=sQuery(id+"F16.wireOp",VERTEX,"E34.0.14.0");
            var Q17;
            Q17=sQuery(id+"F16.wireOp",VERTEX,"E33.1.0.0");
            var Q18;
            Q18=sQuery(id+"F16.wireOp",VERTEX,"E34.0.5.0");
            var Q19;
            Q19=sQuery(id+"F16.wireOp",VERTEX,"E34.0.15.0");
            var Q20;
            Q20=sQuery(id+"F16.wireOp",VERTEX,"E34.0.19.0");
            var Q21;
            Q21=sQuery(id+"F16.wireOp",VERTEX,"E34.0.3.0");
            var Q22;
            Q22=sQuery(id+"F16.wireOp",VERTEX,"E34.0.7.0");
            var Q23;
            Q23=sQuery(id+"F16.wireOp",VERTEX,"E34.0.11.0");
            var Q24;
            Q24=sQuery(id+"F16.wireOp",VERTEX,"E34.0.21.0");
            var Q25;
            Q25=sQuery(id+"F16.wireOp",VERTEX,"E34.0.20.0");
            var Q26;
            Q26=sQuery(id+"F16.wireOp",VERTEX,"E34.0.27.0");
            var Q27;
            Q27=sQuery(id+"F16.wireOp",VERTEX,"E34.0.23.0");
            var Q28;
            Q28=sQuery(id+"F16.wireOp",VERTEX,"E33.2.0.0");
            var Q29;
            Q29=sQuery(id+"F16.wireOp",VERTEX,"E34.0.28.0");
            var Q30;
            Q30=sQuery(id+"F16.wireOp",VERTEX,"E34.0.53.0");
            var Q31;
            Q31=sQuery(id+"F16.wireOp",VERTEX,"E34.0.32.0");
            var Q32;
            Q32=sQuery(id+"F16.wireOp",VERTEX,"E34.0.36.0");
            var Q33;
            Q33=sQuery(id+"F16.wireOp",VERTEX,"E34.0.58.0");
            var Q34;
            Q34=sQuery(id+"F16.wireOp",VERTEX,"E34.0.54.0");
            var Q35;
            Q35=sQuery(id+"F16.wireOp",VERTEX,"E34.0.37.0");
            var Q36;
            Q36=sQuery(id+"F16.wireOp",VERTEX,"E34.0.57.0");
            var Q37;
            Q37=sQuery(id+"F16.wireOp",VERTEX,"E34.0.52.0");
            var Q38;
            Q38=sQuery(id+"F16.wireOp",VERTEX,"E34.0.30.0");
            var Q39;
            Q39=sQuery(id+"F16.wireOp",VERTEX,"E34.0.60.0");
            var Q40;
            Q40=sQuery(id+"F16.wireOp",VERTEX,"E34.0.40.0");
            var Q41;
            Q41=sQuery(id+"F16.wireOp",VERTEX,"E34.0.45.0");
            var Q42;
            Q42=sQuery(id+"F16.wireOp",VERTEX,"E34.0.44.0");
            var Q43;
            Q43=sQuery(id+"F16.wireOp",VERTEX,"E34.0.50.0");
            var Q44;
            Q44=sQuery(id+"F16.wireOp",VERTEX,"E34.0.49.0");
            var Q45;
            Q45=sQuery(id+"F16.wireOp",VERTEX,"E34.0.55.0");
            var Q46;
            Q46=sQuery(id+"F16.wireOp",VERTEX,"E34.0.38.0");
            var Q47;
            Q47=sQuery(id+"F16.wireOp",VERTEX,"E34.0.47.0");
            var Q48;
            Q48=sQuery(id+"F16.wireOp",VERTEX,"E34.0.63.0");
            var Q49;
            Q49=sQuery(id+"F16.wireOp",VERTEX,"E34.0.34.0");
            var Q50;
            Q50=sQuery(id+"F16.wireOp",VERTEX,"E34.0.56.0");
            var Q51;
            Q51=sQuery(id+"F16.wireOp",VERTEX,"E34.0.33.0");
            var Q52;
            Q52=sQuery(id+"F16.wireOp",VERTEX,"E34.0.46.0");
            var Q53;
            Q53=sQuery(id+"F16.wireOp",VERTEX,"E34.0.48.0");
            var Q54;
            Q54=sQuery(id+"F16.wireOp",VERTEX,"E34.0.61.0");
            var Q55;
            Q55=sQuery(id+"F16.wireOp",VERTEX,"E34.0.43.0");
            var Q56;
            Q56=sQuery(id+"F16.wireOp",VERTEX,"E34.0.42.0");
            var Q57;
            Q57=sQuery(id+"F16.wireOp",VERTEX,"E34.0.35.0");
            var Q58;
            Q58=sQuery(id+"F16.wireOp",VERTEX,"E34.0.59.0");
            var Q59;
            Q59=sQuery(id+"F16.wireOp",VERTEX,"E34.0.31.0");
            var Q60;
            Q60=sQuery(id+"F16.wireOp",VERTEX,"E34.0.51.0");
            var Q61;
            Q61=sQuery(id+"F16.wireOp",VERTEX,"E34.0.62.0");
            var Q62;
            Q62=sQuery(id+"F16.wireOp",VERTEX,"E34.0.41.0");
            var Q63;
            Q63=sQuery(id+"F16.wireOp",VERTEX,"E34.0.39.0");
            var Q64;
            Q64=sQuery(id+"F16.wireOp",VERTEX,"E34.0.64.0");
            var Q65;
            Q65=sQuery(id+"F16.wireOp",VERTEX,"E34.0.77.0");
            var Q66;
            Q66=sQuery(id+"F16.wireOp",VERTEX,"E34.0.68.0");
            var Q67;
            Q67=sQuery(id+"F16.wireOp",VERTEX,"E34.0.74.0");
            var Q68;
            Q68=sQuery(id+"F16.wireOp",VERTEX,"E34.0.66.0");
            var Q69;
            Q69=sQuery(id+"F16.wireOp",VERTEX,"E34.0.79.0");
            var Q70;
            Q70=sQuery(id+"F16.wireOp",VERTEX,"E34.0.65.0");
            var Q71;
            Q71=sQuery(id+"F16.wireOp",VERTEX,"E34.0.72.0");
            var Q72;
            Q72=sQuery(id+"F16.wireOp",VERTEX,"E34.0.78.0");
            var Q73;
            Q73=sQuery(id+"F16.wireOp",VERTEX,"E34.0.70.0");
            var Q74;
            Q74=sQuery(id+"F16.wireOp",VERTEX,"E34.0.76.0");
            var Q75;
            Q75=sQuery(id+"F16.wireOp",VERTEX,"E34.0.71.0");
            var Q76;
            Q76=sQuery(id+"F16.wireOp",VERTEX,"E34.0.69.0");
            var Q77;
            Q77=sQuery(id+"F16.wireOp",VERTEX,"E34.0.73.0");
            var Q78;
            Q78=sQuery(id+"F16.wireOp",VERTEX,"E34.0.75.0");
            var Q79;
            Q79=sQuery(id+"F16.wireOp",VERTEX,"E34.0.67.0");
            var Q80;
            Q80=makeQuery(id+"F15.opExtrude","SWEPT_BODY",BODY,{"disambiguationData":[OSD([sQuery(id+"F0.wireOp",EDGE,"E25.3.14.0"),sQuery(id+"F0.wireOp",EDGE,"E25.6.14.0"),sQuery(id+"F0.wireOp",EDGE,"E25.9.14.0"),sQuery(id+"F0.wireOp",EDGE,"E25.12.14.0"),sQuery(id+"F0.wireOp",EDGE,"E25.21.14.0"),sQuery(id+"F0.wireOp",EDGE,"E25.24.14.0"),sQuery(id+"F0.wireOp",EDGE,"E25.27.14.0"),sQuery(id+"F0.wireOp",EDGE,"E25.30.14.0"),sQuery(id+"F0.wireOp",EDGE,"E25.33.14.0"),sQuery(id+"F0.wireOp",EDGE,"E25.36.14.0"),sQuery(id+"F0.wireOp",EDGE,"E25.43.14.0"),sQuery(id+"F0.wireOp",EDGE,"E25.46.14.0"),sQuery(id+"F0.wireOp",EDGE,"E25.49.14.0"),sQuery(id+"F0.wireOp",EDGE,"E25.52.14.0"),sQuery(id+"F0.wireOp",EDGE,"E25.56.14.0"),sQuery(id+"F0.wireOp",EDGE,"E25.59.14.0"),sQuery(id+"F0.wireOp",EDGE,"E25.63.14.0"),sQuery(id+"F0.wireOp",EDGE,"E25.66.14.0"),sQuery(id+"F0.wireOp",EDGE,"E25.70.14.0"),sQuery(id+"F0.wireOp",EDGE,"E25.74.14.0")])]});
            hole(context, id + "F19", {"style" : HoleStyle.C_BORE, "endStyle" : HoleEndStyle.THROUGH, "holeDiameter" : 3.5 * mm, "cBoreDiameter" : 6 * mm, "cBoreDepth" : 4.5 * mm, "majorDiameter" : 5 * mm, "isTappedThrough" : true, "tappedDepth" : 12 * mm, "tapClearance" : 3, "locations" : qUnion([Q0, Q1, Q2, Q3, Q4, Q5, Q6, Q7, Q8, Q9, Q10, Q11, Q12, Q13, Q14, Q15, Q16, Q17, Q18, Q19, Q20, Q21, Q22, Q23, Q24, Q25, Q26, Q27, Q28, Q29, Q30, Q31, Q32, Q33, Q34, Q35, Q36, Q37, Q38, Q39, Q40, Q41, Q42, Q43, Q44, Q45, Q46, Q47, Q48, Q49, Q50, Q51, Q52, Q53, Q54, Q55, Q56, Q57, Q58, Q59, Q60, Q61, Q62, Q63, Q64, Q65, Q66, Q67, Q68, Q69, Q70, Q71, Q72, Q73, Q74, Q75, Q76, Q77, Q78, Q79]), "scope" : qUnion([Q80])});
        }
        {
            var Q0;
            Q0=qCreatedBy(makeId("Front.planeOp"),FACE);
            var sketch = newSketch(context, id + "F20", { "sketchPlane" : qUnion([Q0])});
            skLineSegment(sketch, "E35", {"start": v(-50, 0) * mm, "end": v(-50, 9) * mm, "construction": true});
            skLineSegment(sketch, "E36", {"start": v(-50, 9) * mm, "end": v(-63.5, 9) * mm});
            skLineSegment(sketch, "E37", {"start": v(-63.5, 9) * mm, "end": v(-63.5, -1) * mm});
            skLineSegment(sketch, "E38", {"start": v(-63.5, -1) * mm, "end": v(-56, -1) * mm});
            skLineSegment(sketch, "E39", {"start": v(-56, -1) * mm, "end": v(-56, -0.1) * mm});
            skLineSegment(sketch, "E40", {"start": v(-56, 4) * mm, "end": v(-50, 4) * mm});
            skPoint(sketch, "E41", {"position": v(-60, 9) * mm});
            skLineSegment(sketch, "E42", {"start": v(-4.45, 1.3) * mm, "end": v(-56, 1.3) * mm, "construction": true});
            skArc(sketch, "E43", {"start": v(-56, 2.7) * mm, "mid": v(-57.4, 1.3) * mm, "end": v(-56, -0.1) * mm});
            skLineSegment(sketch, "E44.MirrorCS", {"start": v(-50, 9) * mm, "end": v(-36.5, 9) * mm});
            skPoint(sketch, "E45.MirrorP", {"position": v(-40, 9) * mm});
            skLineSegment(sketch, "E46.MirrorCS", {"start": v(-36.5, 9) * mm, "end": v(-36.5, -1) * mm});
            skLineSegment(sketch, "E47.MirrorCS", {"start": v(-36.5, -1) * mm, "end": v(-44, -1) * mm});
            skArc(sketch, "E48.MirrorCS", {"start": v(-44, 2.7) * mm, "mid": v(-42.6, 1.3) * mm, "end": v(-44, -0.1) * mm});
            skLineSegment(sketch, "E49", {"start": v(-56, -0.1) * mm, "end": v(-56, 2.7) * mm});
            skLineSegment(sketch, "E50", {"start": v(-56, 2.7) * mm, "end": v(-56, 4) * mm});
            skLineSegment(sketch, "E51", {"start": v(-5.5, -4) * mm, "end": v(-63.5, -4) * mm, "construction": true});
            skLineSegment(sketch, "E52.MirrorCS", {"start": v(-44, 4) * mm, "end": v(-50, 4) * mm});
            skLineSegment(sketch, "E53.MirrorCS", {"start": v(-44, 2.7) * mm, "end": v(-44, 4) * mm});
            skLineSegment(sketch, "E54.MirrorCS", {"start": v(-44, -1) * mm, "end": v(-44, -0.1) * mm});
            skPoint(sketch, "E55", {"position": v(-50, 6.5) * mm});
            skLineSegment(sketch, "E56", {"start": v(-63.5, 8.5) * mm, "end": v(-36.5, 8.5) * mm});
            skLineSegment(sketch, "E57.MirrorCS", {"start": v(-62, 0) * mm, "end": v(-62, 9) * mm, "construction": true});
            skLineSegment(sketch, "E58.MirrorCS", {"start": v(-44, -0.1) * mm, "end": v(-44, 2.7) * mm});
            skLineSegment(sketch, "E59.1.0.0", {"start": v(-90, 0) * mm, "end": v(-90, 9) * mm, "construction": true});
            skArc(sketch, "E59.1.0.1", {"start": v(-96, 2.7) * mm, "mid": v(-97.4, 1.3) * mm, "end": v(-96, -0.1) * mm});
            skArc(sketch, "E59.1.0.2", {"start": v(-84, 2.7) * mm, "mid": v(-82.6, 1.3) * mm, "end": v(-84, -0.1) * mm});
            skLineSegment(sketch, "E59.1.0.3", {"start": v(-96, -0.1) * mm, "end": v(-96, 2.7) * mm});
            skLineSegment(sketch, "E59.1.0.4", {"start": v(-96, 2.7) * mm, "end": v(-96, 4) * mm});
            skLineSegment(sketch, "E59.1.0.5", {"start": v(-96, -1) * mm, "end": v(-96, -0.1) * mm});
            skLineSegment(sketch, "E59.1.0.6", {"start": v(-96, 4) * mm, "end": v(-90, 4) * mm});
            skLineSegment(sketch, "E59.1.0.7", {"start": v(-76.5, -1) * mm, "end": v(-84, -1) * mm});
            skLineSegment(sketch, "E59.1.0.8", {"start": v(-84, 4) * mm, "end": v(-90, 4) * mm});
            skLineSegment(sketch, "E59.1.0.9", {"start": v(-84, 2.7) * mm, "end": v(-84, 4) * mm});
            skLineSegment(sketch, "E59.1.0.10", {"start": v(-84, -0.1) * mm, "end": v(-84, 2.7) * mm});
            skLineSegment(sketch, "E59.1.0.11", {"start": v(-84, -1) * mm, "end": v(-84, -0.1) * mm});
            skLineSegment(sketch, "E59.1.0.12", {"start": v(-76.5, 9) * mm, "end": v(-76.5, -1) * mm});
            skLineSegment(sketch, "E59.1.0.13", {"start": v(-103.5, -1) * mm, "end": v(-96, -1) * mm});
            skLineSegment(sketch, "E59.1.0.14", {"start": v(-103.5, 9) * mm, "end": v(-103.5, -1) * mm});
            skLineSegment(sketch, "E59.1.0.15", {"start": v(-103.5, 8.5) * mm, "end": v(-76.5, 8.5) * mm});
            skLineSegment(sketch, "E59.1.0.16", {"start": v(-90, 9) * mm, "end": v(-103.5, 9) * mm});
            skLineSegment(sketch, "E59.1.0.17", {"start": v(-90, 9) * mm, "end": v(-76.5, 9) * mm});
            skPoint(sketch, "E59.1.0.18", {"position": v(-80, 9) * mm});
            skPoint(sketch, "E59.1.0.19", {"position": v(-100, 9) * mm});
            skPoint(sketch, "E59.1.0.20", {"position": v(-90, 6.5) * mm});
            skLineSegment(sketch, "E59.direction1", {"start": v(-50, 0) * mm, "end": v(-90, 0) * mm, "construction": true});
            skSolve(sketch);
        }
        {
            var Q0;
            {var subQ3=sQuery(id+"F20.wireOp",EDGE,"E38");Q0=makeQuery(id+"F20.imprint","IMPRINT",FACE,{"disambiguationData":[TD([[makeQuery(id+"F20.imprint","IMPRINT",EDGE,{"derivedFrom":subQ3}),1.0]])]});}
            var Q1;
            {var subQ4=sQuery(id+"F20.wireOp",EDGE,"E36");Q1=makeQuery(id+"F20.imprint","IMPRINT",FACE,{"disambiguationData":[TD([[makeQuery(id+"F20.imprint","IMPRINT",EDGE,{"derivedFrom":subQ4}),1.0]])]});}
            extrude(context, id + "F21", {"entities" : qUnion([Q0, Q1]), "depth" : 21.7 / 2 * mm, "offsetDistance" : 25 * mm});
        }
        {
            var Q0;
            Q0=makeQuery(id+"F21.opExtrude","CAP_FACE",FACE,{"disambiguationData":[OSD([sQuery(id+"F20.wireOp",EDGE,"E36"),sQuery(id+"F20.wireOp",EDGE,"E37"),sQuery(id+"F20.wireOp",EDGE,"E38"),sQuery(id+"F20.wireOp",EDGE,"E39"),sQuery(id+"F20.wireOp",EDGE,"E40"),sQuery(id+"F20.wireOp",EDGE,"E43"),sQuery(id+"F20.wireOp",EDGE,"E44.MirrorCS"),sQuery(id+"F20.wireOp",EDGE,"E46.MirrorCS"),sQuery(id+"F20.wireOp",EDGE,"E47.MirrorCS"),sQuery(id+"F20.wireOp",EDGE,"E48.MirrorCS"),sQuery(id+"F20.wireOp",EDGE,"E50"),sQuery(id+"F20.wireOp",EDGE,"E52.MirrorCS"),sQuery(id+"F20.wireOp",EDGE,"E53.MirrorCS"),sQuery(id+"F20.wireOp",EDGE,"E54.MirrorCS")])],"isStart":false});
            var sketch = newSketch(context, id + "F22", { "sketchPlane" : qUnion([Q0])});
            skLineSegment(sketch, "E60.0", {"start": v(-63.5, 8.5) * mm, "end": v(-36.5, 8.5) * mm});
            skLineSegment(sketch, "E61.0", {"start": v(-56, -0.1) * mm, "end": v(-56, 2.7) * mm});
            skLineSegment(sketch, "E62.0", {"start": v(-44, -0.1) * mm, "end": v(-44, 2.7) * mm});
            skSolve(sketch);
        }
        {
            var Q0;
            {var subQ1=sQuery(id+"F22.wireOp",EDGE,"E60.0");Q0=makeQuery(id+"F22.imprint","IMPRINT",FACE,{"disambiguationData":[TD([[makeQuery(id+"F22.imprint","IMPRINT",EDGE,{"derivedFrom":subQ1}),-1.0]])]});}
            var Q1;
            Q1=makeQuery(id+"F22.imprint","IMPRINT",FACE,{"disambiguationData":[TD([[makeQuery(id+"F22.imprint","IMPRINT",EDGE,{"derivedFrom":sQuery(id+"F22.wireOp",EDGE,"E61.0")}),1.0]])]});
            var Q2;
            Q2=makeQuery(id+"F22.imprint","IMPRINT",FACE,{"disambiguationData":[TD([[makeQuery(id+"F22.imprint","IMPRINT",EDGE,{"derivedFrom":sQuery(id+"F22.wireOp",EDGE,"E62.0")}),-1.0]])]});
            extrude(context, id + "F23", {"entities" : qUnion([Q0, Q1, Q2]), "operationType" : NewBodyOperationType.ADD, "depth" : ((34.7 - 21.7) / 2) * mm, "offsetDistance" : 25 * mm});
        }
        {
            var Q0;
            Q0=makeQuery(id+"F20.imprint","IMPRINT",FACE,{"disambiguationData":[TD([[makeQuery(id+"F20.imprint","IMPRINT",EDGE,{"derivedFrom":sQuery(id+"F20.wireOp",EDGE,"E59.1.0.1")}),-1.0]])]});
            var Q1;
            {var subQ2=sQuery(id+"F20.wireOp",EDGE,"E59.1.0.15");Q1=makeQuery(id+"F20.imprint","IMPRINT",FACE,{"disambiguationData":[TD([[makeQuery(id+"F20.imprint","IMPRINT",EDGE,{"derivedFrom":subQ2}),1.0]])]});}
            extrude(context, id + "F24", {"entities" : qUnion([Q0, Q1]), "depth" : (32.4 / 2) * mm, "offsetDistance" : 25 * mm});
        }
        {
            var Q0;
            Q0=makeQuery(id+"F24.opExtrude","CAP_FACE",FACE,{"disambiguationData":[OSD([sQuery(id+"F20.wireOp",EDGE,"E59.1.0.1"),sQuery(id+"F20.wireOp",EDGE,"E59.1.0.2"),sQuery(id+"F20.wireOp",EDGE,"E59.1.0.4"),sQuery(id+"F20.wireOp",EDGE,"E59.1.0.5"),sQuery(id+"F20.wireOp",EDGE,"E59.1.0.6"),sQuery(id+"F20.wireOp",EDGE,"E59.1.0.7"),sQuery(id+"F20.wireOp",EDGE,"E59.1.0.8"),sQuery(id+"F20.wireOp",EDGE,"E59.1.0.9"),sQuery(id+"F20.wireOp",EDGE,"E59.1.0.11"),sQuery(id+"F20.wireOp",EDGE,"E59.1.0.12"),sQuery(id+"F20.wireOp",EDGE,"E59.1.0.13"),sQuery(id+"F20.wireOp",EDGE,"E59.1.0.14"),sQuery(id+"F20.wireOp",EDGE,"E59.1.0.16"),sQuery(id+"F20.wireOp",EDGE,"E59.1.0.17")])],"isStart":false});
            var sketch = newSketch(context, id + "F25", { "sketchPlane" : qUnion([Q0])});
            skLineSegment(sketch, "E63.0", {"start": v(-103.5, 8.5) * mm, "end": v(-76.5, 8.5) * mm});
            skLineSegment(sketch, "E64.0", {"start": v(-84, -0.1) * mm, "end": v(-84, 2.7) * mm});
            skLineSegment(sketch, "E65.0", {"start": v(-96, -0.1) * mm, "end": v(-96, 2.7) * mm});
            skSolve(sketch);
        }
        {
            var Q0;
            {var subQ2=sQuery(id+"F25.wireOp",EDGE,"E63.0");Q0=makeQuery(id+"F25.imprint","IMPRINT",FACE,{"disambiguationData":[TD([[makeQuery(id+"F25.imprint","IMPRINT",EDGE,{"derivedFrom":subQ2}),-1.0]])]});}
            var Q1;
            Q1=makeQuery(id+"F25.imprint","IMPRINT",FACE,{"disambiguationData":[TD([[makeQuery(id+"F25.imprint","IMPRINT",EDGE,{"derivedFrom":sQuery(id+"F25.wireOp",EDGE,"E65.0")}),1.0]])]});
            var Q2;
            Q2=makeQuery(id+"F25.imprint","IMPRINT",FACE,{"disambiguationData":[TD([[makeQuery(id+"F25.imprint","IMPRINT",EDGE,{"derivedFrom":sQuery(id+"F25.wireOp",EDGE,"E64.0")}),-1.0]])]});
            extrude(context, id + "F26", {"entities" : qUnion([Q0, Q1, Q2]), "operationType" : NewBodyOperationType.ADD, "depth" : ((45.4 - 32.4) / 2) * mm, "offsetDistance" : 25 * mm});
        }
        {
            var Q0;
            Q0=makeQuery(id+"F24.opExtrude","SWEPT_FACE",FACE,{"disambiguationData":[OSD([sQuery(id+"F20.wireOp",EDGE,"E59.1.0.16"),sQuery(id+"F20.wireOp",EDGE,"E59.1.0.17")])]});
            var sketch = newSketch(context, id + "F27", { "sketchPlane" : qUnion([Q0])});
            skPoint(sketch, "E66.0", {"position": v(-100, 0) * mm});
            skPoint(sketch, "E66.1", {"position": v(-80, 0) * mm});
            skPoint(sketch, "E67.0", {"position": v(-60, 0) * mm});
            skPoint(sketch, "E68.0", {"position": v(-40, 0) * mm});
            skPoint(sketch, "E69", {"position": v(-100, -10) * mm});
            skPoint(sketch, "E70", {"position": v(-80, -10) * mm});
            skPoint(sketch, "E71", {"position": v(-60, -7.5) * mm});
            skPoint(sketch, "E72", {"position": v(-40, -7.5) * mm});
            skSolve(sketch);
        }
        {
            var Q0;
            Q0=sQuery(id+"F27.wireOp",VERTEX,"E69");
            var Q1;
            Q1=sQuery(id+"F27.wireOp",VERTEX,"E70");
            var Q2;
            Q2=sQuery(id+"F27.wireOp",VERTEX,"E71");
            var Q3;
            Q3=sQuery(id+"F27.wireOp",VERTEX,"E72");
            var Q4;
            Q4=makeQuery(id+"F21.opExtrude","SWEPT_BODY",BODY,{"disambiguationData":[OSD([sQuery(id+"F20.wireOp",EDGE,"E36"),sQuery(id+"F20.wireOp",EDGE,"E37"),sQuery(id+"F20.wireOp",EDGE,"E38"),sQuery(id+"F20.wireOp",EDGE,"E39"),sQuery(id+"F20.wireOp",EDGE,"E40"),sQuery(id+"F20.wireOp",EDGE,"E43"),sQuery(id+"F20.wireOp",EDGE,"E44.MirrorCS"),sQuery(id+"F20.wireOp",EDGE,"E46.MirrorCS"),sQuery(id+"F20.wireOp",EDGE,"E47.MirrorCS"),sQuery(id+"F20.wireOp",EDGE,"E48.MirrorCS"),sQuery(id+"F20.wireOp",EDGE,"E50"),sQuery(id+"F20.wireOp",EDGE,"E52.MirrorCS"),sQuery(id+"F20.wireOp",EDGE,"E53.MirrorCS"),sQuery(id+"F20.wireOp",EDGE,"E54.MirrorCS")])]});
            var Q5;
            Q5=makeQuery(id+"F24.opExtrude","SWEPT_BODY",BODY,{"disambiguationData":[OSD([sQuery(id+"F20.wireOp",EDGE,"E59.1.0.1"),sQuery(id+"F20.wireOp",EDGE,"E59.1.0.2"),sQuery(id+"F20.wireOp",EDGE,"E59.1.0.4"),sQuery(id+"F20.wireOp",EDGE,"E59.1.0.5"),sQuery(id+"F20.wireOp",EDGE,"E59.1.0.6"),sQuery(id+"F20.wireOp",EDGE,"E59.1.0.7"),sQuery(id+"F20.wireOp",EDGE,"E59.1.0.8"),sQuery(id+"F20.wireOp",EDGE,"E59.1.0.9"),sQuery(id+"F20.wireOp",EDGE,"E59.1.0.11"),sQuery(id+"F20.wireOp",EDGE,"E59.1.0.12"),sQuery(id+"F20.wireOp",EDGE,"E59.1.0.13"),sQuery(id+"F20.wireOp",EDGE,"E59.1.0.14"),sQuery(id+"F20.wireOp",EDGE,"E59.1.0.16"),sQuery(id+"F20.wireOp",EDGE,"E59.1.0.17")])]});
            hole(context, id + "F28", {"style" : HoleStyle.SIMPLE, "endStyle" : HoleEndStyle.BLIND, "standardTappedOrClearance" : lookupTablePath({ "standard" : "ISO", "engagement" : "75%", "pitch" : "0.5 mm", "size" : "M3", "type" : "Tapped" }), "standardBlindInLast" : lookupTablePath({ "standard" : "ISO", "engagement" : "75%", "pitch" : "0.5 mm", "size" : "M3", "type" : "Tapped" }), "holeDiameter" : 2.5 * mm, "majorDiameter" : 3 * mm, "showTappedDepth" : true, "holeDepth" : 5 * mm, "isTappedThrough" : true, "tappedDepth" : 3.5 * mm, "tapClearance" : 3, "locations" : qUnion([Q0, Q1, Q2, Q3]), "scope" : qUnion([Q4, Q5])});
        }
        {
            var Q0;
            Q0=makeQuery(id+"F24.opExtrude","CAP_EDGE",EDGE,{"disambiguationData":[OSD([sQuery(id+"F20.wireOp",EDGE,"E59.1.0.16"),sQuery(id+"F20.wireOp",EDGE,"E59.1.0.17")])],"isStart":false});
            var Q1;
            Q1=makeQuery(id+"F24.opExtrude","SWEPT_EDGE",EDGE,{"disambiguationData":[OSD([sQuery(id+"F20.wireOp",EDGE,"E59.1.0.12"),sQuery(id+"F20.wireOp",EDGE,"E59.1.0.17")])]});
            var Q2;
            Q2=makeQuery(id+"F26.opExtrude","CAP_EDGE",EDGE,{"disambiguationData":[OSD([sQuery(id+"F25.wireOp",EDGE,"E63.0")])],"isStart":false});
            var Q3;
            Q3=makeQuery(id+"F24.opExtrude","SWEPT_EDGE",EDGE,{"disambiguationData":[OSD([sQuery(id+"F20.wireOp",EDGE,"E59.1.0.14"),sQuery(id+"F20.wireOp",EDGE,"E59.1.0.16")])]});
            var Q4;
            Q4=makeQuery(id+"F23.opExtrude","CAP_EDGE",EDGE,{"disambiguationData":[OSD([sQuery(id+"F22.wireOp",EDGE,"E60.0")])],"isStart":false});
            var Q5;
            Q5=makeQuery(id+"F21.opExtrude","CAP_EDGE",EDGE,{"disambiguationData":[OSD([sQuery(id+"F20.wireOp",EDGE,"E36"),sQuery(id+"F20.wireOp",EDGE,"E44.MirrorCS")])],"isStart":false});
            var Q6;
            Q6=makeQuery(id+"F21.opExtrude","SWEPT_EDGE",EDGE,{"disambiguationData":[OSD([sQuery(id+"F20.wireOp",EDGE,"E36"),sQuery(id+"F20.wireOp",EDGE,"E37")])]});
            var Q7;
            Q7=makeQuery(id+"F21.opExtrude","SWEPT_EDGE",EDGE,{"disambiguationData":[OSD([sQuery(id+"F20.wireOp",EDGE,"E44.MirrorCS"),sQuery(id+"F20.wireOp",EDGE,"E46.MirrorCS")])]});
            chamfer(context, id + "F29", {"entities" : qUnion([Q0, Q1, Q2, Q3, Q4, Q5, Q6, Q7]), "width" : 0.5 * mm, "tangentPropagation" : true});
        }
        {
            var Q0;
            Q0=makeQuery(id+"F21.opExtrude","SWEPT_BODY",BODY,{"disambiguationData":[OSD([sQuery(id+"F20.wireOp",EDGE,"E36"),sQuery(id+"F20.wireOp",EDGE,"E37"),sQuery(id+"F20.wireOp",EDGE,"E38"),sQuery(id+"F20.wireOp",EDGE,"E39"),sQuery(id+"F20.wireOp",EDGE,"E40"),sQuery(id+"F20.wireOp",EDGE,"E43"),sQuery(id+"F20.wireOp",EDGE,"E44.MirrorCS"),sQuery(id+"F20.wireOp",EDGE,"E46.MirrorCS"),sQuery(id+"F20.wireOp",EDGE,"E47.MirrorCS"),sQuery(id+"F20.wireOp",EDGE,"E48.MirrorCS"),sQuery(id+"F20.wireOp",EDGE,"E50"),sQuery(id+"F20.wireOp",EDGE,"E52.MirrorCS"),sQuery(id+"F20.wireOp",EDGE,"E53.MirrorCS"),sQuery(id+"F20.wireOp",EDGE,"E54.MirrorCS")])]});
            var Q1;
            Q1=makeQuery(id+"F24.opExtrude","SWEPT_BODY",BODY,{"disambiguationData":[OSD([sQuery(id+"F20.wireOp",EDGE,"E59.1.0.1"),sQuery(id+"F20.wireOp",EDGE,"E59.1.0.2"),sQuery(id+"F20.wireOp",EDGE,"E59.1.0.4"),sQuery(id+"F20.wireOp",EDGE,"E59.1.0.5"),sQuery(id+"F20.wireOp",EDGE,"E59.1.0.6"),sQuery(id+"F20.wireOp",EDGE,"E59.1.0.7"),sQuery(id+"F20.wireOp",EDGE,"E59.1.0.8"),sQuery(id+"F20.wireOp",EDGE,"E59.1.0.9"),sQuery(id+"F20.wireOp",EDGE,"E59.1.0.11"),sQuery(id+"F20.wireOp",EDGE,"E59.1.0.12"),sQuery(id+"F20.wireOp",EDGE,"E59.1.0.13"),sQuery(id+"F20.wireOp",EDGE,"E59.1.0.14"),sQuery(id+"F20.wireOp",EDGE,"E59.1.0.16"),sQuery(id+"F20.wireOp",EDGE,"E59.1.0.17")])]});
            var Q2;
            Q2=makeQuery(id+"F20.imprint","IMPRINT",FACE,{"disambiguationData":[TD([[makeQuery(id+"F20.imprint","IMPRINT",EDGE,{"derivedFrom":sQuery(id+"F20.wireOp",EDGE,"E59.1.0.1")}),-1.0]])]});
            mirror(context, id + "F30", {"operationType" : NewBodyOperationType.ADD, "entities" : qUnion([Q0, Q1]), "mirrorPlane" : qUnion([Q2])});
        }
    });
